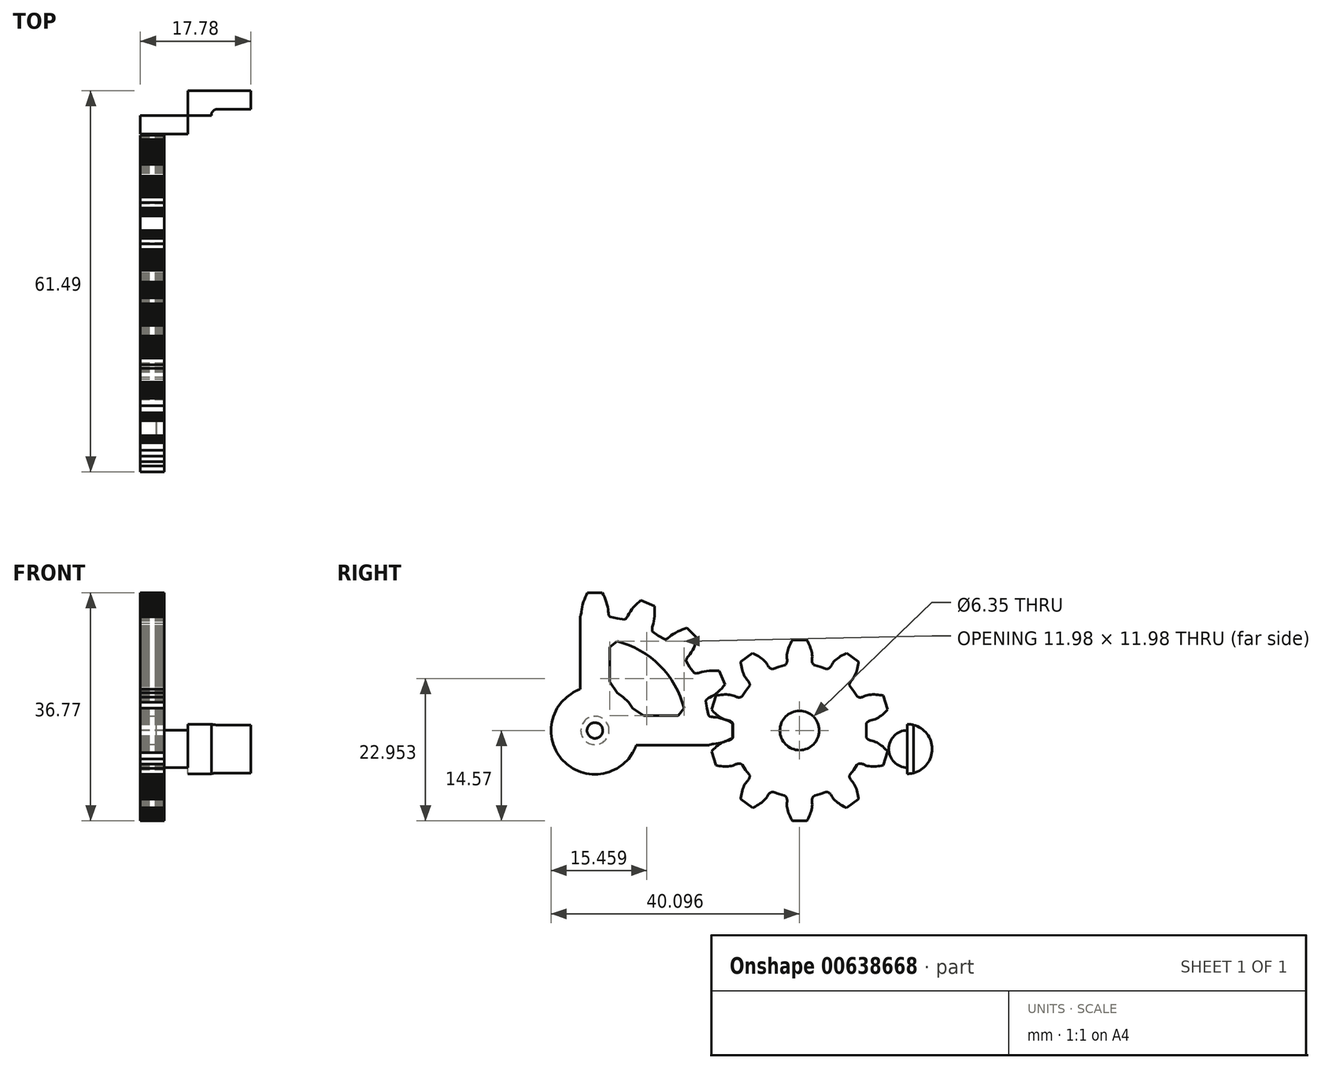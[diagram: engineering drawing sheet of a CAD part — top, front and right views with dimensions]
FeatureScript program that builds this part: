
annotation { "Feature Type Name" : "Feature", "Feature Type Description" : "" }
export const myFeature = defineFeature(function(context is Context, id is Id, definition is map)
    precondition{}
    {
        {
            var Q0;
            Q0=qCreatedBy(makeId("Right.planeOp"),FACE);
            var sketch = newSketch(context, id + "F0", { "sketchPlane" : qUnion([Q0])});
            skLineSegment(sketch, "E0", {"start": v(-32.36, 6.57) * mm, "end": v(-32.07, 5.41) * mm});
            skLineSegment(sketch, "E1", {"start": v(-32.07, 5.41) * mm, "end": v(-31.97, 5.33) * mm});
            skLineSegment(sketch, "E2", {"start": v(-31.97, 5.33) * mm, "end": v(-31.86, 5.27) * mm});
            skLineSegment(sketch, "E3", {"start": v(-31.86, 5.27) * mm, "end": v(-31.66, 5.2) * mm});
            skLineSegment(sketch, "E4", {"start": v(-31.66, 5.2) * mm, "end": v(-31.46, 5.16) * mm});
            skLineSegment(sketch, "E5", {"start": v(-31.46, 5.16) * mm, "end": v(-31.27, 5.14) * mm});
            skLineSegment(sketch, "E6", {"start": v(-31.27, 5.14) * mm, "end": v(-30.88, 5.1) * mm});
            skLineSegment(sketch, "E7", {"start": v(-30.88, 5.1) * mm, "end": v(-30.49, 5.04) * mm});
            skLineSegment(sketch, "E8", {"start": v(-30.49, 5.04) * mm, "end": v(-30.1, 4.95) * mm});
            skLineSegment(sketch, "E9", {"start": v(-30.1, 4.95) * mm, "end": v(-29.7, 4.83) * mm});
            skLineSegment(sketch, "E10", {"start": v(-29.7, 4.83) * mm, "end": v(-29.3, 4.68) * mm});
            skLineSegment(sketch, "E11", {"start": v(-29.3, 4.68) * mm, "end": v(-28.9, 4.52) * mm});
            skLineSegment(sketch, "E12", {"start": v(-28.9, 4.52) * mm, "end": v(-28.5, 4.34) * mm});
            skLineSegment(sketch, "E13", {"start": v(-28.5, 4.34) * mm, "end": v(-28.21, 4.19) * mm});
            skLineSegment(sketch, "E14", {"start": v(-28.21, 4.19) * mm, "end": v(-28.21, 1.77) * mm});
            skLineSegment(sketch, "E15", {"start": v(-28.21, 1.77) * mm, "end": v(-28.5, 1.62) * mm});
            skLineSegment(sketch, "E16", {"start": v(-28.5, 1.62) * mm, "end": v(-28.9, 1.44) * mm});
            skLineSegment(sketch, "E17", {"start": v(-28.9, 1.44) * mm, "end": v(-29.3, 1.28) * mm});
            skLineSegment(sketch, "E18", {"start": v(-29.3, 1.28) * mm, "end": v(-29.7, 1.13) * mm});
            skLineSegment(sketch, "E19", {"start": v(-29.7, 1.13) * mm, "end": v(-30.1, 1.01) * mm});
            skLineSegment(sketch, "E20", {"start": v(-30.1, 1.01) * mm, "end": v(-30.49, 0.92) * mm});
            skLineSegment(sketch, "E21", {"start": v(-30.49, 0.92) * mm, "end": v(-30.88, 0.85) * mm});
            skLineSegment(sketch, "E22", {"start": v(-30.88, 0.85) * mm, "end": v(-31.27, 0.82) * mm});
            skLineSegment(sketch, "E23", {"start": v(-31.27, 0.82) * mm, "end": v(-31.46, 0.8) * mm});
            skLineSegment(sketch, "E24", {"start": v(-31.46, 0.8) * mm, "end": v(-31.66, 0.76) * mm});
            skLineSegment(sketch, "E25", {"start": v(-31.66, 0.76) * mm, "end": v(-31.86, 0.69) * mm});
            skLineSegment(sketch, "E26", {"start": v(-31.86, 0.69) * mm, "end": v(-31.97, 0.63) * mm});
            skLineSegment(sketch, "E27", {"start": v(-31.97, 0.63) * mm, "end": v(-32.07, 0.55) * mm});
            skLineSegment(sketch, "E28", {"start": v(-32.07, 0.55) * mm, "end": v(-32.36, -0.61) * mm});
            skLineSegment(sketch, "E29", {"start": v(-32.36, -0.61) * mm, "end": v(-32.54, -1.79) * mm});
            skLineSegment(sketch, "E30", {"start": v(-32.54, -1.79) * mm, "end": v(-32.47, -1.9) * mm});
            skLineSegment(sketch, "E31", {"start": v(-32.47, -1.9) * mm, "end": v(-32.4, -2) * mm});
            skLineSegment(sketch, "E32", {"start": v(-32.4, -2) * mm, "end": v(-32.24, -2.15) * mm});
            skLineSegment(sketch, "E33", {"start": v(-32.24, -2.15) * mm, "end": v(-32.07, -2.26) * mm});
            skLineSegment(sketch, "E34", {"start": v(-32.07, -2.26) * mm, "end": v(-31.9, -2.35) * mm});
            skLineSegment(sketch, "E35", {"start": v(-31.9, -2.35) * mm, "end": v(-31.55, -2.53) * mm});
            skLineSegment(sketch, "E36", {"start": v(-31.55, -2.53) * mm, "end": v(-31.22, -2.74) * mm});
            skLineSegment(sketch, "E37", {"start": v(-31.22, -2.74) * mm, "end": v(-30.89, -2.98) * mm});
            skLineSegment(sketch, "E38", {"start": v(-30.89, -2.98) * mm, "end": v(-30.57, -3.24) * mm});
            skLineSegment(sketch, "E39", {"start": v(-30.57, -3.24) * mm, "end": v(-30.26, -3.52) * mm});
            skLineSegment(sketch, "E40", {"start": v(-30.26, -3.52) * mm, "end": v(-29.95, -3.83) * mm});
            skLineSegment(sketch, "E41", {"start": v(-29.95, -3.83) * mm, "end": v(-29.66, -4.15) * mm});
            skLineSegment(sketch, "E42", {"start": v(-29.66, -4.15) * mm, "end": v(-29.44, -4.4) * mm});
            skLineSegment(sketch, "E43", {"start": v(-29.44, -4.4) * mm, "end": v(-30.37, -6.63) * mm});
            skLineSegment(sketch, "E44", {"start": v(-30.37, -6.63) * mm, "end": v(-30.7, -6.66) * mm});
            skLineSegment(sketch, "E45", {"start": v(-30.7, -6.66) * mm, "end": v(-31.13, -6.68) * mm});
            skLineSegment(sketch, "E46", {"start": v(-31.13, -6.68) * mm, "end": v(-31.56, -6.67) * mm});
            skLineSegment(sketch, "E47", {"start": v(-31.56, -6.67) * mm, "end": v(-31.98, -6.65) * mm});
            skLineSegment(sketch, "E48", {"start": v(-31.98, -6.65) * mm, "end": v(-32.4, -6.61) * mm});
            skLineSegment(sketch, "E49", {"start": v(-32.4, -6.61) * mm, "end": v(-32.8, -6.55) * mm});
            skLineSegment(sketch, "E50", {"start": v(-32.8, -6.55) * mm, "end": v(-33.18, -6.46) * mm});
            skLineSegment(sketch, "E51", {"start": v(-33.18, -6.46) * mm, "end": v(-33.55, -6.34) * mm});
            skLineSegment(sketch, "E52", {"start": v(-33.55, -6.34) * mm, "end": v(-33.74, -6.28) * mm});
            skLineSegment(sketch, "E53", {"start": v(-33.74, -6.28) * mm, "end": v(-33.94, -6.25) * mm});
            skLineSegment(sketch, "E54", {"start": v(-33.94, -6.25) * mm, "end": v(-34.15, -6.24) * mm});
            skLineSegment(sketch, "E55", {"start": v(-34.15, -6.24) * mm, "end": v(-34.27, -6.25) * mm});
            skLineSegment(sketch, "E56", {"start": v(-34.27, -6.25) * mm, "end": v(-34.4, -6.29) * mm});
            skLineSegment(sketch, "E57", {"start": v(-34.4, -6.29) * mm, "end": v(-35.11, -7.25) * mm});
            skLineSegment(sketch, "E58", {"start": v(-35.11, -7.25) * mm, "end": v(-35.72, -8.27) * mm});
            skLineSegment(sketch, "E59", {"start": v(-35.72, -8.27) * mm, "end": v(-35.7, -8.4) * mm});
            skLineSegment(sketch, "E60", {"start": v(-35.7, -8.4) * mm, "end": v(-35.68, -8.52) * mm});
            skLineSegment(sketch, "E61", {"start": v(-35.68, -8.52) * mm, "end": v(-35.58, -8.71) * mm});
            skLineSegment(sketch, "E62", {"start": v(-35.58, -8.71) * mm, "end": v(-35.47, -8.88) * mm});
            skLineSegment(sketch, "E63", {"start": v(-35.47, -8.88) * mm, "end": v(-35.35, -9.03) * mm});
            skLineSegment(sketch, "E64", {"start": v(-35.35, -9.03) * mm, "end": v(-35.1, -9.33) * mm});
            skLineSegment(sketch, "E65", {"start": v(-35.1, -9.33) * mm, "end": v(-34.87, -9.65) * mm});
            skLineSegment(sketch, "E66", {"start": v(-34.87, -9.65) * mm, "end": v(-34.66, -10) * mm});
            skLineSegment(sketch, "E67", {"start": v(-34.66, -10) * mm, "end": v(-34.46, -10.36) * mm});
            skLineSegment(sketch, "E68", {"start": v(-34.46, -10.36) * mm, "end": v(-34.28, -10.74) * mm});
            skLineSegment(sketch, "E69", {"start": v(-34.28, -10.74) * mm, "end": v(-34.11, -11.14) * mm});
            skLineSegment(sketch, "E70", {"start": v(-34.11, -11.14) * mm, "end": v(-33.96, -11.55) * mm});
            skLineSegment(sketch, "E71", {"start": v(-33.96, -11.55) * mm, "end": v(-33.86, -11.86) * mm});
            skLineSegment(sketch, "E72", {"start": v(-33.86, -11.86) * mm, "end": v(-35.57, -13.57) * mm});
            skLineSegment(sketch, "E73", {"start": v(-35.57, -13.57) * mm, "end": v(-35.89, -13.47) * mm});
            skLineSegment(sketch, "E74", {"start": v(-35.89, -13.47) * mm, "end": v(-36.3, -13.32) * mm});
            skLineSegment(sketch, "E75", {"start": v(-36.3, -13.32) * mm, "end": v(-36.7, -13.15) * mm});
            skLineSegment(sketch, "E76", {"start": v(-36.7, -13.15) * mm, "end": v(-37.07, -12.97) * mm});
            skLineSegment(sketch, "E77", {"start": v(-37.07, -12.97) * mm, "end": v(-37.43, -12.78) * mm});
            skLineSegment(sketch, "E78", {"start": v(-37.43, -12.78) * mm, "end": v(-37.78, -12.57) * mm});
            skLineSegment(sketch, "E79", {"start": v(-37.78, -12.57) * mm, "end": v(-38.1, -12.34) * mm});
            skLineSegment(sketch, "E80", {"start": v(-38.1, -12.34) * mm, "end": v(-38.4, -12.08) * mm});
            skLineSegment(sketch, "E81", {"start": v(-38.4, -12.08) * mm, "end": v(-38.55, -11.96) * mm});
            skLineSegment(sketch, "E82", {"start": v(-38.55, -11.96) * mm, "end": v(-38.72, -11.85) * mm});
            skLineSegment(sketch, "E83", {"start": v(-38.72, -11.85) * mm, "end": v(-38.92, -11.76) * mm});
            skLineSegment(sketch, "E84", {"start": v(-38.92, -11.76) * mm, "end": v(-39.03, -11.73) * mm});
            skLineSegment(sketch, "E85", {"start": v(-39.03, -11.73) * mm, "end": v(-39.17, -11.71) * mm});
            skLineSegment(sketch, "E86", {"start": v(-39.17, -11.71) * mm, "end": v(-40.19, -12.32) * mm});
            skLineSegment(sketch, "E87", {"start": v(-40.19, -12.32) * mm, "end": v(-41.15, -13.03) * mm});
            skLineSegment(sketch, "E88", {"start": v(-41.15, -13.03) * mm, "end": v(-41.18, -13.17) * mm});
            skLineSegment(sketch, "E89", {"start": v(-41.18, -13.17) * mm, "end": v(-41.2, -13.28) * mm});
            skLineSegment(sketch, "E90", {"start": v(-41.2, -13.28) * mm, "end": v(-41.19, -13.5) * mm});
            skLineSegment(sketch, "E91", {"start": v(-41.19, -13.5) * mm, "end": v(-41.15, -13.7) * mm});
            skLineSegment(sketch, "E92", {"start": v(-41.15, -13.7) * mm, "end": v(-41.1, -13.88) * mm});
            skLineSegment(sketch, "E93", {"start": v(-41.1, -13.88) * mm, "end": v(-40.97, -14.25) * mm});
            skLineSegment(sketch, "E94", {"start": v(-40.97, -14.25) * mm, "end": v(-40.88, -14.64) * mm});
            skLineSegment(sketch, "E95", {"start": v(-40.88, -14.64) * mm, "end": v(-40.82, -15.04) * mm});
            skLineSegment(sketch, "E96", {"start": v(-40.82, -15.04) * mm, "end": v(-40.78, -15.45) * mm});
            skLineSegment(sketch, "E97", {"start": v(-40.78, -15.45) * mm, "end": v(-40.76, -15.87) * mm});
            skLineSegment(sketch, "E98", {"start": v(-40.76, -15.87) * mm, "end": v(-40.76, -16.3) * mm});
            skLineSegment(sketch, "E99", {"start": v(-40.76, -16.3) * mm, "end": v(-40.78, -16.74) * mm});
            skLineSegment(sketch, "E100", {"start": v(-40.78, -16.74) * mm, "end": v(-40.8, -17.07) * mm});
            skLineSegment(sketch, "E101", {"start": v(-40.8, -17.07) * mm, "end": v(-43.03, -18) * mm});
            skLineSegment(sketch, "E102", {"start": v(-43.03, -18) * mm, "end": v(-43.29, -17.78) * mm});
            skLineSegment(sketch, "E103", {"start": v(-43.29, -17.78) * mm, "end": v(-43.6, -17.48) * mm});
            skLineSegment(sketch, "E104", {"start": v(-43.6, -17.48) * mm, "end": v(-43.9, -17.18) * mm});
            skLineSegment(sketch, "E105", {"start": v(-43.9, -17.18) * mm, "end": v(-44.2, -16.87) * mm});
            skLineSegment(sketch, "E106", {"start": v(-44.2, -16.87) * mm, "end": v(-44.45, -16.55) * mm});
            skLineSegment(sketch, "E107", {"start": v(-44.45, -16.55) * mm, "end": v(-44.7, -16.22) * mm});
            skLineSegment(sketch, "E108", {"start": v(-44.7, -16.22) * mm, "end": v(-44.9, -15.88) * mm});
            skLineSegment(sketch, "E109", {"start": v(-44.9, -15.88) * mm, "end": v(-45.08, -15.53) * mm});
            skLineSegment(sketch, "E110", {"start": v(-45.08, -15.53) * mm, "end": v(-45.17, -15.36) * mm});
            skLineSegment(sketch, "E111", {"start": v(-45.17, -15.36) * mm, "end": v(-45.29, -15.2) * mm});
            skLineSegment(sketch, "E112", {"start": v(-45.29, -15.2) * mm, "end": v(-45.43, -15.04) * mm});
            skLineSegment(sketch, "E113", {"start": v(-45.43, -15.04) * mm, "end": v(-45.52, -14.96) * mm});
            skLineSegment(sketch, "E114", {"start": v(-45.52, -14.96) * mm, "end": v(-45.64, -14.9) * mm});
            skLineSegment(sketch, "E115", {"start": v(-45.64, -14.9) * mm, "end": v(-46.82, -15.07) * mm});
            skLineSegment(sketch, "E116", {"start": v(-46.82, -15.07) * mm, "end": v(-47.98, -15.36) * mm});
            skLineSegment(sketch, "E117", {"start": v(-47.98, -15.36) * mm, "end": v(-48.06, -15.47) * mm});
            skLineSegment(sketch, "E118", {"start": v(-48.06, -15.47) * mm, "end": v(-48.12, -15.57) * mm});
            skLineSegment(sketch, "E119", {"start": v(-48.12, -15.57) * mm, "end": v(-48.2, -15.77) * mm});
            skLineSegment(sketch, "E120", {"start": v(-48.2, -15.77) * mm, "end": v(-48.24, -15.97) * mm});
            skLineSegment(sketch, "E121", {"start": v(-48.24, -15.97) * mm, "end": v(-48.26, -16.17) * mm});
            skLineSegment(sketch, "E122", {"start": v(-48.26, -16.17) * mm, "end": v(-48.29, -16.55) * mm});
            skLineSegment(sketch, "E123", {"start": v(-48.29, -16.55) * mm, "end": v(-48.35, -16.95) * mm});
            skLineSegment(sketch, "E124", {"start": v(-48.35, -16.95) * mm, "end": v(-48.45, -17.34) * mm});
            skLineSegment(sketch, "E125", {"start": v(-48.45, -17.34) * mm, "end": v(-48.57, -17.74) * mm});
            skLineSegment(sketch, "E126", {"start": v(-48.57, -17.74) * mm, "end": v(-48.7, -18.13) * mm});
            skLineSegment(sketch, "E127", {"start": v(-48.7, -18.13) * mm, "end": v(-48.87, -18.53) * mm});
            skLineSegment(sketch, "E128", {"start": v(-48.87, -18.53) * mm, "end": v(-49.06, -18.93) * mm});
            skLineSegment(sketch, "E129", {"start": v(-49.06, -18.93) * mm, "end": v(-49.2, -19.22) * mm});
            skLineSegment(sketch, "E130", {"start": v(-49.2, -19.22) * mm, "end": v(-51.62, -19.22) * mm});
            skLineSegment(sketch, "E131", {"start": v(-51.62, -19.22) * mm, "end": v(-51.77, -18.93) * mm});
            skLineSegment(sketch, "E132", {"start": v(-51.77, -18.93) * mm, "end": v(-51.96, -18.53) * mm});
            skLineSegment(sketch, "E133", {"start": v(-51.96, -18.53) * mm, "end": v(-52.12, -18.13) * mm});
            skLineSegment(sketch, "E134", {"start": v(-52.12, -18.13) * mm, "end": v(-52.26, -17.74) * mm});
            skLineSegment(sketch, "E135", {"start": v(-52.26, -17.74) * mm, "end": v(-52.38, -17.34) * mm});
            skLineSegment(sketch, "E136", {"start": v(-52.38, -17.34) * mm, "end": v(-52.47, -16.95) * mm});
            skLineSegment(sketch, "E137", {"start": v(-52.47, -16.95) * mm, "end": v(-52.54, -16.55) * mm});
            skLineSegment(sketch, "E138", {"start": v(-52.54, -16.55) * mm, "end": v(-52.57, -16.17) * mm});
            skLineSegment(sketch, "E139", {"start": v(-52.57, -16.17) * mm, "end": v(-52.6, -15.97) * mm});
            skLineSegment(sketch, "E140", {"start": v(-52.6, -15.97) * mm, "end": v(-52.63, -15.77) * mm});
            skLineSegment(sketch, "E141", {"start": v(-52.63, -15.77) * mm, "end": v(-52.7, -15.57) * mm});
            skLineSegment(sketch, "E142", {"start": v(-52.7, -15.57) * mm, "end": v(-52.76, -15.47) * mm});
            skLineSegment(sketch, "E143", {"start": v(-52.76, -15.47) * mm, "end": v(-52.85, -15.36) * mm});
            skLineSegment(sketch, "E144", {"start": v(-52.85, -15.36) * mm, "end": v(-54, -15.07) * mm});
            skLineSegment(sketch, "E145", {"start": v(-54, -15.07) * mm, "end": v(-55.18, -14.9) * mm});
            skLineSegment(sketch, "E146", {"start": v(-55.18, -14.9) * mm, "end": v(-55.3, -14.96) * mm});
            skLineSegment(sketch, "E147", {"start": v(-55.3, -14.96) * mm, "end": v(-55.4, -15.04) * mm});
            skLineSegment(sketch, "E148", {"start": v(-55.4, -15.04) * mm, "end": v(-55.54, -15.2) * mm});
            skLineSegment(sketch, "E149", {"start": v(-55.54, -15.2) * mm, "end": v(-55.65, -15.36) * mm});
            skLineSegment(sketch, "E150", {"start": v(-55.65, -15.36) * mm, "end": v(-55.75, -15.53) * mm});
            skLineSegment(sketch, "E151", {"start": v(-55.75, -15.53) * mm, "end": v(-55.92, -15.88) * mm});
            skLineSegment(sketch, "E152", {"start": v(-55.92, -15.88) * mm, "end": v(-56.14, -16.22) * mm});
            skLineSegment(sketch, "E153", {"start": v(-56.14, -16.22) * mm, "end": v(-56.37, -16.55) * mm});
            skLineSegment(sketch, "E154", {"start": v(-56.37, -16.55) * mm, "end": v(-56.64, -16.87) * mm});
            skLineSegment(sketch, "E155", {"start": v(-56.64, -16.87) * mm, "end": v(-56.92, -17.18) * mm});
            skLineSegment(sketch, "E156", {"start": v(-56.92, -17.18) * mm, "end": v(-57.22, -17.48) * mm});
            skLineSegment(sketch, "E157", {"start": v(-57.22, -17.48) * mm, "end": v(-57.54, -17.78) * mm});
            skLineSegment(sketch, "E158", {"start": v(-57.54, -17.78) * mm, "end": v(-57.8, -18) * mm});
            skLineSegment(sketch, "E159", {"start": v(-57.8, -18) * mm, "end": v(-60.03, -17.07) * mm});
            skLineSegment(sketch, "E160", {"start": v(-60.03, -17.07) * mm, "end": v(-60.05, -16.74) * mm});
            skLineSegment(sketch, "E161", {"start": v(-60.05, -16.74) * mm, "end": v(-60.07, -16.3) * mm});
            skLineSegment(sketch, "E162", {"start": v(-60.07, -16.3) * mm, "end": v(-60.07, -15.87) * mm});
            skLineSegment(sketch, "E163", {"start": v(-60.07, -15.87) * mm, "end": v(-60.05, -15.45) * mm});
            skLineSegment(sketch, "E164", {"start": v(-60.05, -15.45) * mm, "end": v(-60, -15.04) * mm});
            skLineSegment(sketch, "E165", {"start": v(-60, -15.04) * mm, "end": v(-59.94, -14.64) * mm});
            skLineSegment(sketch, "E166", {"start": v(-59.94, -14.64) * mm, "end": v(-59.85, -14.25) * mm});
            skLineSegment(sketch, "E167", {"start": v(-59.85, -14.25) * mm, "end": v(-59.74, -13.88) * mm});
            skLineSegment(sketch, "E168", {"start": v(-59.74, -13.88) * mm, "end": v(-59.68, -13.7) * mm});
            skLineSegment(sketch, "E169", {"start": v(-59.68, -13.7) * mm, "end": v(-59.64, -13.5) * mm});
            skLineSegment(sketch, "E170", {"start": v(-59.64, -13.5) * mm, "end": v(-59.63, -13.28) * mm});
            skLineSegment(sketch, "E171", {"start": v(-59.63, -13.28) * mm, "end": v(-59.64, -13.17) * mm});
            skLineSegment(sketch, "E172", {"start": v(-59.64, -13.17) * mm, "end": v(-59.68, -13.03) * mm});
            skLineSegment(sketch, "E173", {"start": v(-59.68, -13.03) * mm, "end": v(-60.64, -12.32) * mm});
            skLineSegment(sketch, "E174", {"start": v(-60.64, -12.32) * mm, "end": v(-61.66, -11.71) * mm});
            skLineSegment(sketch, "E175", {"start": v(-61.66, -11.71) * mm, "end": v(-61.8, -11.73) * mm});
            skLineSegment(sketch, "E176", {"start": v(-61.8, -11.73) * mm, "end": v(-61.91, -11.76) * mm});
            skLineSegment(sketch, "E177", {"start": v(-61.91, -11.76) * mm, "end": v(-62.1, -11.85) * mm});
            skLineSegment(sketch, "E178", {"start": v(-62.1, -11.85) * mm, "end": v(-62.27, -11.96) * mm});
            skLineSegment(sketch, "E179", {"start": v(-62.27, -11.96) * mm, "end": v(-62.43, -12.08) * mm});
            skLineSegment(sketch, "E180", {"start": v(-62.43, -12.08) * mm, "end": v(-62.72, -12.34) * mm});
            skLineSegment(sketch, "E181", {"start": v(-62.72, -12.34) * mm, "end": v(-63.05, -12.57) * mm});
            skLineSegment(sketch, "E182", {"start": v(-63.05, -12.57) * mm, "end": v(-63.4, -12.78) * mm});
            skLineSegment(sketch, "E183", {"start": v(-63.4, -12.78) * mm, "end": v(-63.76, -12.97) * mm});
            skLineSegment(sketch, "E184", {"start": v(-63.76, -12.97) * mm, "end": v(-64.14, -13.15) * mm});
            skLineSegment(sketch, "E185", {"start": v(-64.14, -13.15) * mm, "end": v(-64.53, -13.32) * mm});
            skLineSegment(sketch, "E186", {"start": v(-64.53, -13.32) * mm, "end": v(-64.94, -13.47) * mm});
            skLineSegment(sketch, "E187", {"start": v(-64.94, -13.47) * mm, "end": v(-65.26, -13.57) * mm});
            skLineSegment(sketch, "E188", {"start": v(-65.26, -13.57) * mm, "end": v(-66.97, -11.86) * mm});
            skLineSegment(sketch, "E189", {"start": v(-66.97, -11.86) * mm, "end": v(-66.86, -11.55) * mm});
            skLineSegment(sketch, "E190", {"start": v(-66.86, -11.55) * mm, "end": v(-66.71, -11.14) * mm});
            skLineSegment(sketch, "E191", {"start": v(-66.71, -11.14) * mm, "end": v(-66.55, -10.74) * mm});
            skLineSegment(sketch, "E192", {"start": v(-66.55, -10.74) * mm, "end": v(-66.37, -10.36) * mm});
            skLineSegment(sketch, "E193", {"start": v(-66.37, -10.36) * mm, "end": v(-66.17, -10) * mm});
            skLineSegment(sketch, "E194", {"start": v(-66.17, -10) * mm, "end": v(-65.96, -9.65) * mm});
            skLineSegment(sketch, "E195", {"start": v(-65.96, -9.65) * mm, "end": v(-65.73, -9.33) * mm});
            skLineSegment(sketch, "E196", {"start": v(-65.73, -9.33) * mm, "end": v(-65.48, -9.03) * mm});
            skLineSegment(sketch, "E197", {"start": v(-65.48, -9.03) * mm, "end": v(-65.35, -8.88) * mm});
            skLineSegment(sketch, "E198", {"start": v(-65.35, -8.88) * mm, "end": v(-65.24, -8.71) * mm});
            skLineSegment(sketch, "E199", {"start": v(-65.24, -8.71) * mm, "end": v(-65.15, -8.52) * mm});
            skLineSegment(sketch, "E200", {"start": v(-65.15, -8.52) * mm, "end": v(-65.12, -8.4) * mm});
            skLineSegment(sketch, "E201", {"start": v(-65.12, -8.4) * mm, "end": v(-65.1, -8.27) * mm});
            skLineSegment(sketch, "E202", {"start": v(-65.1, -8.27) * mm, "end": v(-65.72, -7.25) * mm});
            skLineSegment(sketch, "E203", {"start": v(-65.72, -7.25) * mm, "end": v(-66.43, -6.29) * mm});
            skLineSegment(sketch, "E204", {"start": v(-66.43, -6.29) * mm, "end": v(-66.56, -6.25) * mm});
            skLineSegment(sketch, "E205", {"start": v(-66.56, -6.25) * mm, "end": v(-66.68, -6.24) * mm});
            skLineSegment(sketch, "E206", {"start": v(-66.68, -6.24) * mm, "end": v(-66.9, -6.25) * mm});
            skLineSegment(sketch, "E207", {"start": v(-66.9, -6.25) * mm, "end": v(-67.09, -6.28) * mm});
            skLineSegment(sketch, "E208", {"start": v(-67.09, -6.28) * mm, "end": v(-67.28, -6.34) * mm});
            skLineSegment(sketch, "E209", {"start": v(-67.28, -6.34) * mm, "end": v(-67.65, -6.46) * mm});
            skLineSegment(sketch, "E210", {"start": v(-67.65, -6.46) * mm, "end": v(-68.04, -6.55) * mm});
            skLineSegment(sketch, "E211", {"start": v(-68.04, -6.55) * mm, "end": v(-68.44, -6.61) * mm});
            skLineSegment(sketch, "E212", {"start": v(-68.44, -6.61) * mm, "end": v(-68.85, -6.65) * mm});
            skLineSegment(sketch, "E213", {"start": v(-68.85, -6.65) * mm, "end": v(-69.27, -6.67) * mm});
            skLineSegment(sketch, "E214", {"start": v(-69.27, -6.67) * mm, "end": v(-69.7, -6.68) * mm});
            skLineSegment(sketch, "E215", {"start": v(-69.7, -6.68) * mm, "end": v(-70.13, -6.66) * mm});
            skLineSegment(sketch, "E216", {"start": v(-70.13, -6.66) * mm, "end": v(-70.46, -6.63) * mm});
            skLineSegment(sketch, "E217", {"start": v(-70.46, -6.63) * mm, "end": v(-71.39, -4.4) * mm});
            skLineSegment(sketch, "E218", {"start": v(-71.39, -4.4) * mm, "end": v(-71.17, -4.15) * mm});
            skLineSegment(sketch, "E219", {"start": v(-71.17, -4.15) * mm, "end": v(-70.88, -3.83) * mm});
            skLineSegment(sketch, "E220", {"start": v(-70.88, -3.83) * mm, "end": v(-70.57, -3.52) * mm});
            skLineSegment(sketch, "E221", {"start": v(-70.57, -3.52) * mm, "end": v(-70.26, -3.24) * mm});
            skLineSegment(sketch, "E222", {"start": v(-70.26, -3.24) * mm, "end": v(-69.94, -2.98) * mm});
            skLineSegment(sketch, "E223", {"start": v(-69.94, -2.98) * mm, "end": v(-69.61, -2.74) * mm});
            skLineSegment(sketch, "E224", {"start": v(-69.61, -2.74) * mm, "end": v(-69.28, -2.53) * mm});
            skLineSegment(sketch, "E225", {"start": v(-69.28, -2.53) * mm, "end": v(-68.93, -2.35) * mm});
            skLineSegment(sketch, "E226", {"start": v(-68.93, -2.35) * mm, "end": v(-68.76, -2.26) * mm});
            skLineSegment(sketch, "E227", {"start": v(-68.76, -2.26) * mm, "end": v(-68.59, -2.15) * mm});
            skLineSegment(sketch, "E228", {"start": v(-68.59, -2.15) * mm, "end": v(-68.43, -2) * mm});
            skLineSegment(sketch, "E229", {"start": v(-68.43, -2) * mm, "end": v(-68.36, -1.9) * mm});
            skLineSegment(sketch, "E230", {"start": v(-68.36, -1.9) * mm, "end": v(-68.3, -1.79) * mm});
            skLineSegment(sketch, "E231", {"start": v(-68.3, -1.79) * mm, "end": v(-68.47, -0.61) * mm});
            skLineSegment(sketch, "E232", {"start": v(-68.47, -0.61) * mm, "end": v(-68.75, 0.55) * mm});
            skLineSegment(sketch, "E233", {"start": v(-68.75, 0.55) * mm, "end": v(-68.86, 0.63) * mm});
            skLineSegment(sketch, "E234", {"start": v(-68.86, 0.63) * mm, "end": v(-68.97, 0.69) * mm});
            skLineSegment(sketch, "E235", {"start": v(-68.97, 0.69) * mm, "end": v(-69.17, 0.76) * mm});
            skLineSegment(sketch, "E236", {"start": v(-69.17, 0.76) * mm, "end": v(-69.36, 0.8) * mm});
            skLineSegment(sketch, "E237", {"start": v(-69.36, 0.8) * mm, "end": v(-69.56, 0.82) * mm});
            skLineSegment(sketch, "E238", {"start": v(-69.56, 0.82) * mm, "end": v(-69.95, 0.85) * mm});
            skLineSegment(sketch, "E239", {"start": v(-69.95, 0.85) * mm, "end": v(-70.34, 0.92) * mm});
            skLineSegment(sketch, "E240", {"start": v(-70.34, 0.92) * mm, "end": v(-70.74, 1.01) * mm});
            skLineSegment(sketch, "E241", {"start": v(-70.74, 1.01) * mm, "end": v(-71.13, 1.13) * mm});
            skLineSegment(sketch, "E242", {"start": v(-71.13, 1.13) * mm, "end": v(-71.53, 1.28) * mm});
            skLineSegment(sketch, "E243", {"start": v(-71.53, 1.28) * mm, "end": v(-71.92, 1.44) * mm});
            skLineSegment(sketch, "E244", {"start": v(-71.92, 1.44) * mm, "end": v(-72.32, 1.62) * mm});
            skLineSegment(sketch, "E245", {"start": v(-72.32, 1.62) * mm, "end": v(-72.62, 1.77) * mm});
            skLineSegment(sketch, "E246", {"start": v(-72.62, 1.77) * mm, "end": v(-72.62, 4.19) * mm});
            skLineSegment(sketch, "E247", {"start": v(-72.62, 4.19) * mm, "end": v(-72.32, 4.34) * mm});
            skLineSegment(sketch, "E248", {"start": v(-72.32, 4.34) * mm, "end": v(-71.92, 4.52) * mm});
            skLineSegment(sketch, "E249", {"start": v(-71.92, 4.52) * mm, "end": v(-71.53, 4.68) * mm});
            skLineSegment(sketch, "E250", {"start": v(-71.53, 4.68) * mm, "end": v(-71.13, 4.83) * mm});
            skLineSegment(sketch, "E251", {"start": v(-71.13, 4.83) * mm, "end": v(-70.74, 4.95) * mm});
            skLineSegment(sketch, "E252", {"start": v(-70.74, 4.95) * mm, "end": v(-70.34, 5.04) * mm});
            skLineSegment(sketch, "E253", {"start": v(-70.34, 5.04) * mm, "end": v(-69.95, 5.1) * mm});
            skLineSegment(sketch, "E254", {"start": v(-69.95, 5.1) * mm, "end": v(-69.56, 5.14) * mm});
            skLineSegment(sketch, "E255", {"start": v(-69.56, 5.14) * mm, "end": v(-69.36, 5.16) * mm});
            skLineSegment(sketch, "E256", {"start": v(-69.36, 5.16) * mm, "end": v(-69.17, 5.2) * mm});
            skLineSegment(sketch, "E257", {"start": v(-69.17, 5.2) * mm, "end": v(-68.97, 5.27) * mm});
            skLineSegment(sketch, "E258", {"start": v(-68.97, 5.27) * mm, "end": v(-68.86, 5.33) * mm});
            skLineSegment(sketch, "E259", {"start": v(-68.86, 5.33) * mm, "end": v(-68.75, 5.41) * mm});
            skLineSegment(sketch, "E260", {"start": v(-68.75, 5.41) * mm, "end": v(-68.47, 6.57) * mm});
            skLineSegment(sketch, "E261", {"start": v(-68.47, 6.57) * mm, "end": v(-68.3, 7.75) * mm});
            skLineSegment(sketch, "E262", {"start": v(-68.3, 7.75) * mm, "end": v(-68.36, 7.87) * mm});
            skLineSegment(sketch, "E263", {"start": v(-68.36, 7.87) * mm, "end": v(-68.43, 7.96) * mm});
            skLineSegment(sketch, "E264", {"start": v(-68.43, 7.96) * mm, "end": v(-68.59, 8.1) * mm});
            skLineSegment(sketch, "E265", {"start": v(-68.59, 8.1) * mm, "end": v(-68.76, 8.22) * mm});
            skLineSegment(sketch, "E266", {"start": v(-68.76, 8.22) * mm, "end": v(-68.93, 8.31) * mm});
            skLineSegment(sketch, "E267", {"start": v(-68.93, 8.31) * mm, "end": v(-69.28, 8.5) * mm});
            skLineSegment(sketch, "E268", {"start": v(-69.28, 8.5) * mm, "end": v(-69.61, 8.7) * mm});
            skLineSegment(sketch, "E269", {"start": v(-69.61, 8.7) * mm, "end": v(-69.94, 8.94) * mm});
            skLineSegment(sketch, "E270", {"start": v(-69.94, 8.94) * mm, "end": v(-70.26, 9.2) * mm});
            skLineSegment(sketch, "E271", {"start": v(-70.26, 9.2) * mm, "end": v(-70.57, 9.48) * mm});
            skLineSegment(sketch, "E272", {"start": v(-70.57, 9.48) * mm, "end": v(-70.88, 9.79) * mm});
            skLineSegment(sketch, "E273", {"start": v(-70.88, 9.79) * mm, "end": v(-71.17, 10.1) * mm});
            skLineSegment(sketch, "E274", {"start": v(-71.17, 10.1) * mm, "end": v(-71.39, 10.36) * mm});
            skLineSegment(sketch, "E275", {"start": v(-71.39, 10.36) * mm, "end": v(-70.46, 12.6) * mm});
            skLineSegment(sketch, "E276", {"start": v(-70.46, 12.6) * mm, "end": v(-70.13, 12.62) * mm});
            skLineSegment(sketch, "E277", {"start": v(-70.13, 12.62) * mm, "end": v(-69.7, 12.64) * mm});
            skLineSegment(sketch, "E278", {"start": v(-69.7, 12.64) * mm, "end": v(-69.27, 12.63) * mm});
            skLineSegment(sketch, "E279", {"start": v(-69.27, 12.63) * mm, "end": v(-68.85, 12.61) * mm});
            skLineSegment(sketch, "E280", {"start": v(-68.85, 12.61) * mm, "end": v(-68.44, 12.57) * mm});
            skLineSegment(sketch, "E281", {"start": v(-68.44, 12.57) * mm, "end": v(-68.04, 12.5) * mm});
            skLineSegment(sketch, "E282", {"start": v(-68.04, 12.5) * mm, "end": v(-67.65, 12.42) * mm});
            skLineSegment(sketch, "E283", {"start": v(-67.65, 12.42) * mm, "end": v(-67.28, 12.3) * mm});
            skLineSegment(sketch, "E284", {"start": v(-67.28, 12.3) * mm, "end": v(-67.09, 12.24) * mm});
            skLineSegment(sketch, "E285", {"start": v(-67.09, 12.24) * mm, "end": v(-66.9, 12.2) * mm});
            skLineSegment(sketch, "E286", {"start": v(-66.9, 12.2) * mm, "end": v(-66.68, 12.2) * mm});
            skLineSegment(sketch, "E287", {"start": v(-66.68, 12.2) * mm, "end": v(-66.56, 12.2) * mm});
            skLineSegment(sketch, "E288", {"start": v(-66.56, 12.2) * mm, "end": v(-66.43, 12.25) * mm});
            skLineSegment(sketch, "E289", {"start": v(-66.43, 12.25) * mm, "end": v(-65.72, 13.2) * mm});
            skLineSegment(sketch, "E290", {"start": v(-65.72, 13.2) * mm, "end": v(-65.1, 14.23) * mm});
            skLineSegment(sketch, "E291", {"start": v(-65.1, 14.23) * mm, "end": v(-65.12, 14.36) * mm});
            skLineSegment(sketch, "E292", {"start": v(-65.12, 14.36) * mm, "end": v(-65.15, 14.48) * mm});
            skLineSegment(sketch, "E293", {"start": v(-65.15, 14.48) * mm, "end": v(-65.24, 14.67) * mm});
            skLineSegment(sketch, "E294", {"start": v(-65.24, 14.67) * mm, "end": v(-65.35, 14.84) * mm});
            skLineSegment(sketch, "E295", {"start": v(-65.35, 14.84) * mm, "end": v(-65.48, 15) * mm});
            skLineSegment(sketch, "E296", {"start": v(-65.48, 15) * mm, "end": v(-65.73, 15.29) * mm});
            skLineSegment(sketch, "E297", {"start": v(-65.73, 15.29) * mm, "end": v(-65.96, 15.61) * mm});
            skLineSegment(sketch, "E298", {"start": v(-65.96, 15.61) * mm, "end": v(-66.17, 15.96) * mm});
            skLineSegment(sketch, "E299", {"start": v(-66.17, 15.96) * mm, "end": v(-66.37, 16.32) * mm});
            skLineSegment(sketch, "E300", {"start": v(-66.37, 16.32) * mm, "end": v(-66.55, 16.7) * mm});
            skLineSegment(sketch, "E301", {"start": v(-66.55, 16.7) * mm, "end": v(-66.71, 17.1) * mm});
            skLineSegment(sketch, "E302", {"start": v(-66.71, 17.1) * mm, "end": v(-66.86, 17.5) * mm});
            skLineSegment(sketch, "E303", {"start": v(-66.86, 17.5) * mm, "end": v(-66.97, 17.82) * mm});
            skLineSegment(sketch, "E304", {"start": v(-66.97, 17.82) * mm, "end": v(-65.26, 19.53) * mm});
            skLineSegment(sketch, "E305", {"start": v(-65.26, 19.53) * mm, "end": v(-64.94, 19.43) * mm});
            skLineSegment(sketch, "E306", {"start": v(-64.94, 19.43) * mm, "end": v(-64.53, 19.28) * mm});
            skLineSegment(sketch, "E307", {"start": v(-64.53, 19.28) * mm, "end": v(-64.14, 19.11) * mm});
            skLineSegment(sketch, "E308", {"start": v(-64.14, 19.11) * mm, "end": v(-63.76, 18.93) * mm});
            skLineSegment(sketch, "E309", {"start": v(-63.76, 18.93) * mm, "end": v(-63.4, 18.74) * mm});
            skLineSegment(sketch, "E310", {"start": v(-63.4, 18.74) * mm, "end": v(-63.05, 18.53) * mm});
            skLineSegment(sketch, "E311", {"start": v(-63.05, 18.53) * mm, "end": v(-62.72, 18.3) * mm});
            skLineSegment(sketch, "E312", {"start": v(-62.72, 18.3) * mm, "end": v(-62.43, 18.04) * mm});
            skLineSegment(sketch, "E313", {"start": v(-62.43, 18.04) * mm, "end": v(-62.27, 17.92) * mm});
            skLineSegment(sketch, "E314", {"start": v(-62.27, 17.92) * mm, "end": v(-62.1, 17.8) * mm});
            skLineSegment(sketch, "E315", {"start": v(-62.1, 17.8) * mm, "end": v(-61.91, 17.72) * mm});
            skLineSegment(sketch, "E316", {"start": v(-61.91, 17.72) * mm, "end": v(-61.8, 17.69) * mm});
            skLineSegment(sketch, "E317", {"start": v(-61.8, 17.69) * mm, "end": v(-61.66, 17.67) * mm});
            skLineSegment(sketch, "E318", {"start": v(-61.66, 17.67) * mm, "end": v(-60.64, 18.28) * mm});
            skLineSegment(sketch, "E319", {"start": v(-60.64, 18.28) * mm, "end": v(-59.68, 19) * mm});
            skLineSegment(sketch, "E320", {"start": v(-59.68, 19) * mm, "end": v(-59.64, 19.12) * mm});
            skLineSegment(sketch, "E321", {"start": v(-59.64, 19.12) * mm, "end": v(-59.63, 19.24) * mm});
            skLineSegment(sketch, "E322", {"start": v(-59.63, 19.24) * mm, "end": v(-59.64, 19.46) * mm});
            skLineSegment(sketch, "E323", {"start": v(-59.64, 19.46) * mm, "end": v(-59.68, 19.65) * mm});
            skLineSegment(sketch, "E324", {"start": v(-59.68, 19.65) * mm, "end": v(-59.74, 19.84) * mm});
            skLineSegment(sketch, "E325", {"start": v(-59.74, 19.84) * mm, "end": v(-59.85, 20.21) * mm});
            skLineSegment(sketch, "E326", {"start": v(-59.85, 20.21) * mm, "end": v(-59.94, 20.6) * mm});
            skLineSegment(sketch, "E327", {"start": v(-59.94, 20.6) * mm, "end": v(-60, 21) * mm});
            skLineSegment(sketch, "E328", {"start": v(-60, 21) * mm, "end": v(-60.05, 21.41) * mm});
            skLineSegment(sketch, "E329", {"start": v(-60.05, 21.41) * mm, "end": v(-60.07, 21.83) * mm});
            skLineSegment(sketch, "E330", {"start": v(-60.07, 21.83) * mm, "end": v(-60.07, 22.26) * mm});
            skLineSegment(sketch, "E331", {"start": v(-60.07, 22.26) * mm, "end": v(-60.05, 22.7) * mm});
            skLineSegment(sketch, "E332", {"start": v(-60.05, 22.7) * mm, "end": v(-60.03, 23.03) * mm});
            skLineSegment(sketch, "E333", {"start": v(-60.03, 23.03) * mm, "end": v(-57.8, 23.95) * mm});
            skLineSegment(sketch, "E334", {"start": v(-57.8, 23.95) * mm, "end": v(-57.54, 23.74) * mm});
            skLineSegment(sketch, "E335", {"start": v(-57.54, 23.74) * mm, "end": v(-57.22, 23.44) * mm});
            skLineSegment(sketch, "E336", {"start": v(-57.22, 23.44) * mm, "end": v(-56.92, 23.14) * mm});
            skLineSegment(sketch, "E337", {"start": v(-56.92, 23.14) * mm, "end": v(-56.64, 22.83) * mm});
            skLineSegment(sketch, "E338", {"start": v(-56.64, 22.83) * mm, "end": v(-56.37, 22.5) * mm});
            skLineSegment(sketch, "E339", {"start": v(-56.37, 22.5) * mm, "end": v(-56.14, 22.18) * mm});
            skLineSegment(sketch, "E340", {"start": v(-56.14, 22.18) * mm, "end": v(-55.92, 21.84) * mm});
            skLineSegment(sketch, "E341", {"start": v(-55.92, 21.84) * mm, "end": v(-55.75, 21.5) * mm});
            skLineSegment(sketch, "E342", {"start": v(-55.75, 21.5) * mm, "end": v(-55.65, 21.32) * mm});
            skLineSegment(sketch, "E343", {"start": v(-55.65, 21.32) * mm, "end": v(-55.54, 21.15) * mm});
            skLineSegment(sketch, "E344", {"start": v(-55.54, 21.15) * mm, "end": v(-55.4, 21) * mm});
            skLineSegment(sketch, "E345", {"start": v(-55.4, 21) * mm, "end": v(-55.3, 20.92) * mm});
            skLineSegment(sketch, "E346", {"start": v(-55.3, 20.92) * mm, "end": v(-55.18, 20.86) * mm});
            skLineSegment(sketch, "E347", {"start": v(-55.18, 20.86) * mm, "end": v(-54, 21.03) * mm});
            skLineSegment(sketch, "E348", {"start": v(-54, 21.03) * mm, "end": v(-52.85, 21.32) * mm});
            skLineSegment(sketch, "E349", {"start": v(-52.85, 21.32) * mm, "end": v(-52.76, 21.43) * mm});
            skLineSegment(sketch, "E350", {"start": v(-52.76, 21.43) * mm, "end": v(-52.7, 21.53) * mm});
            skLineSegment(sketch, "E351", {"start": v(-52.7, 21.53) * mm, "end": v(-52.63, 21.73) * mm});
            skLineSegment(sketch, "E352", {"start": v(-52.63, 21.73) * mm, "end": v(-52.6, 21.93) * mm});
            skLineSegment(sketch, "E353", {"start": v(-52.6, 21.93) * mm, "end": v(-52.57, 22.13) * mm});
            skLineSegment(sketch, "E354", {"start": v(-52.57, 22.13) * mm, "end": v(-52.54, 22.51) * mm});
            skLineSegment(sketch, "E355", {"start": v(-52.54, 22.51) * mm, "end": v(-52.47, 22.9) * mm});
            skLineSegment(sketch, "E356", {"start": v(-52.47, 22.9) * mm, "end": v(-52.38, 23.3) * mm});
            skLineSegment(sketch, "E357", {"start": v(-52.38, 23.3) * mm, "end": v(-52.26, 23.7) * mm});
            skLineSegment(sketch, "E358", {"start": v(-52.26, 23.7) * mm, "end": v(-52.12, 24.1) * mm});
            skLineSegment(sketch, "E359", {"start": v(-52.12, 24.1) * mm, "end": v(-51.96, 24.49) * mm});
            skLineSegment(sketch, "E360", {"start": v(-51.96, 24.49) * mm, "end": v(-51.77, 24.88) * mm});
            skLineSegment(sketch, "E361", {"start": v(-51.77, 24.88) * mm, "end": v(-51.62, 25.18) * mm});
            skLineSegment(sketch, "E362", {"start": v(-51.62, 25.18) * mm, "end": v(-49.2, 25.18) * mm});
            skLineSegment(sketch, "E363", {"start": v(-49.2, 25.18) * mm, "end": v(-49.06, 24.88) * mm});
            skLineSegment(sketch, "E364", {"start": v(-49.06, 24.88) * mm, "end": v(-48.87, 24.49) * mm});
            skLineSegment(sketch, "E365", {"start": v(-48.87, 24.49) * mm, "end": v(-48.7, 24.1) * mm});
            skLineSegment(sketch, "E366", {"start": v(-48.7, 24.1) * mm, "end": v(-48.57, 23.7) * mm});
            skLineSegment(sketch, "E367", {"start": v(-48.57, 23.7) * mm, "end": v(-48.45, 23.3) * mm});
            skLineSegment(sketch, "E368", {"start": v(-48.45, 23.3) * mm, "end": v(-48.35, 22.9) * mm});
            skLineSegment(sketch, "E369", {"start": v(-48.35, 22.9) * mm, "end": v(-48.29, 22.51) * mm});
            skLineSegment(sketch, "E370", {"start": v(-48.29, 22.51) * mm, "end": v(-48.26, 22.13) * mm});
            skLineSegment(sketch, "E371", {"start": v(-48.26, 22.13) * mm, "end": v(-48.24, 21.93) * mm});
            skLineSegment(sketch, "E372", {"start": v(-48.24, 21.93) * mm, "end": v(-48.2, 21.73) * mm});
            skLineSegment(sketch, "E373", {"start": v(-48.2, 21.73) * mm, "end": v(-48.12, 21.53) * mm});
            skLineSegment(sketch, "E374", {"start": v(-48.12, 21.53) * mm, "end": v(-48.06, 21.43) * mm});
            skLineSegment(sketch, "E375", {"start": v(-48.06, 21.43) * mm, "end": v(-47.98, 21.32) * mm});
            skLineSegment(sketch, "E376", {"start": v(-47.98, 21.32) * mm, "end": v(-46.82, 21.03) * mm});
            skLineSegment(sketch, "E377", {"start": v(-46.82, 21.03) * mm, "end": v(-45.64, 20.86) * mm});
            skLineSegment(sketch, "E378", {"start": v(-45.64, 20.86) * mm, "end": v(-45.52, 20.92) * mm});
            skLineSegment(sketch, "E379", {"start": v(-45.52, 20.92) * mm, "end": v(-45.43, 21) * mm});
            skLineSegment(sketch, "E380", {"start": v(-45.43, 21) * mm, "end": v(-45.29, 21.15) * mm});
            skLineSegment(sketch, "E381", {"start": v(-45.29, 21.15) * mm, "end": v(-45.17, 21.32) * mm});
            skLineSegment(sketch, "E382", {"start": v(-45.17, 21.32) * mm, "end": v(-45.08, 21.5) * mm});
            skLineSegment(sketch, "E383", {"start": v(-45.08, 21.5) * mm, "end": v(-44.9, 21.84) * mm});
            skLineSegment(sketch, "E384", {"start": v(-44.9, 21.84) * mm, "end": v(-44.7, 22.18) * mm});
            skLineSegment(sketch, "E385", {"start": v(-44.7, 22.18) * mm, "end": v(-44.45, 22.5) * mm});
            skLineSegment(sketch, "E386", {"start": v(-44.45, 22.5) * mm, "end": v(-44.2, 22.83) * mm});
            skLineSegment(sketch, "E387", {"start": v(-44.2, 22.83) * mm, "end": v(-43.9, 23.14) * mm});
            skLineSegment(sketch, "E388", {"start": v(-43.9, 23.14) * mm, "end": v(-43.6, 23.44) * mm});
            skLineSegment(sketch, "E389", {"start": v(-43.6, 23.44) * mm, "end": v(-43.29, 23.74) * mm});
            skLineSegment(sketch, "E390", {"start": v(-43.29, 23.74) * mm, "end": v(-43.03, 23.95) * mm});
            skLineSegment(sketch, "E391", {"start": v(-43.03, 23.95) * mm, "end": v(-40.8, 23.03) * mm});
            skLineSegment(sketch, "E392", {"start": v(-40.8, 23.03) * mm, "end": v(-40.78, 22.7) * mm});
            skLineSegment(sketch, "E393", {"start": v(-40.78, 22.7) * mm, "end": v(-40.76, 22.26) * mm});
            skLineSegment(sketch, "E394", {"start": v(-40.76, 22.26) * mm, "end": v(-40.76, 21.83) * mm});
            skLineSegment(sketch, "E395", {"start": v(-40.76, 21.83) * mm, "end": v(-40.78, 21.41) * mm});
            skLineSegment(sketch, "E396", {"start": v(-40.78, 21.41) * mm, "end": v(-40.82, 21) * mm});
            skLineSegment(sketch, "E397", {"start": v(-40.82, 21) * mm, "end": v(-40.88, 20.6) * mm});
            skLineSegment(sketch, "E398", {"start": v(-40.88, 20.6) * mm, "end": v(-40.97, 20.21) * mm});
            skLineSegment(sketch, "E399", {"start": v(-40.97, 20.21) * mm, "end": v(-41.1, 19.84) * mm});
            skLineSegment(sketch, "E400", {"start": v(-41.1, 19.84) * mm, "end": v(-41.15, 19.65) * mm});
            skLineSegment(sketch, "E401", {"start": v(-41.15, 19.65) * mm, "end": v(-41.19, 19.46) * mm});
            skLineSegment(sketch, "E402", {"start": v(-41.19, 19.46) * mm, "end": v(-41.2, 19.24) * mm});
            skLineSegment(sketch, "E403", {"start": v(-41.2, 19.24) * mm, "end": v(-41.18, 19.12) * mm});
            skLineSegment(sketch, "E404", {"start": v(-41.18, 19.12) * mm, "end": v(-41.15, 19) * mm});
            skLineSegment(sketch, "E405", {"start": v(-41.15, 19) * mm, "end": v(-40.19, 18.28) * mm});
            skLineSegment(sketch, "E406", {"start": v(-40.19, 18.28) * mm, "end": v(-39.17, 17.67) * mm});
            skLineSegment(sketch, "E407", {"start": v(-39.17, 17.67) * mm, "end": v(-39.03, 17.69) * mm});
            skLineSegment(sketch, "E408", {"start": v(-39.03, 17.69) * mm, "end": v(-38.92, 17.72) * mm});
            skLineSegment(sketch, "E409", {"start": v(-38.92, 17.72) * mm, "end": v(-38.72, 17.8) * mm});
            skLineSegment(sketch, "E410", {"start": v(-38.72, 17.8) * mm, "end": v(-38.55, 17.92) * mm});
            skLineSegment(sketch, "E411", {"start": v(-38.55, 17.92) * mm, "end": v(-38.4, 18.04) * mm});
            skLineSegment(sketch, "E412", {"start": v(-38.4, 18.04) * mm, "end": v(-38.1, 18.3) * mm});
            skLineSegment(sketch, "E413", {"start": v(-38.1, 18.3) * mm, "end": v(-37.78, 18.53) * mm});
            skLineSegment(sketch, "E414", {"start": v(-37.78, 18.53) * mm, "end": v(-37.43, 18.74) * mm});
            skLineSegment(sketch, "E415", {"start": v(-37.43, 18.74) * mm, "end": v(-37.07, 18.93) * mm});
            skLineSegment(sketch, "E416", {"start": v(-37.07, 18.93) * mm, "end": v(-36.7, 19.11) * mm});
            skLineSegment(sketch, "E417", {"start": v(-36.7, 19.11) * mm, "end": v(-36.3, 19.28) * mm});
            skLineSegment(sketch, "E418", {"start": v(-36.3, 19.28) * mm, "end": v(-35.89, 19.43) * mm});
            skLineSegment(sketch, "E419", {"start": v(-35.89, 19.43) * mm, "end": v(-35.57, 19.53) * mm});
            skLineSegment(sketch, "E420", {"start": v(-35.57, 19.53) * mm, "end": v(-33.86, 17.82) * mm});
            skLineSegment(sketch, "E421", {"start": v(-33.86, 17.82) * mm, "end": v(-33.96, 17.5) * mm});
            skLineSegment(sketch, "E422", {"start": v(-33.96, 17.5) * mm, "end": v(-34.11, 17.1) * mm});
            skLineSegment(sketch, "E423", {"start": v(-34.11, 17.1) * mm, "end": v(-34.28, 16.7) * mm});
            skLineSegment(sketch, "E424", {"start": v(-34.28, 16.7) * mm, "end": v(-34.46, 16.32) * mm});
            skLineSegment(sketch, "E425", {"start": v(-34.46, 16.32) * mm, "end": v(-34.66, 15.96) * mm});
            skLineSegment(sketch, "E426", {"start": v(-34.66, 15.96) * mm, "end": v(-34.87, 15.61) * mm});
            skLineSegment(sketch, "E427", {"start": v(-34.87, 15.61) * mm, "end": v(-35.1, 15.29) * mm});
            skLineSegment(sketch, "E428", {"start": v(-35.1, 15.29) * mm, "end": v(-35.35, 15) * mm});
            skLineSegment(sketch, "E429", {"start": v(-35.35, 15) * mm, "end": v(-35.47, 14.84) * mm});
            skLineSegment(sketch, "E430", {"start": v(-35.47, 14.84) * mm, "end": v(-35.58, 14.67) * mm});
            skLineSegment(sketch, "E431", {"start": v(-35.58, 14.67) * mm, "end": v(-35.68, 14.48) * mm});
            skLineSegment(sketch, "E432", {"start": v(-35.68, 14.48) * mm, "end": v(-35.7, 14.36) * mm});
            skLineSegment(sketch, "E433", {"start": v(-35.7, 14.36) * mm, "end": v(-35.72, 14.23) * mm});
            skLineSegment(sketch, "E434", {"start": v(-35.72, 14.23) * mm, "end": v(-35.11, 13.2) * mm});
            skLineSegment(sketch, "E435", {"start": v(-35.11, 13.2) * mm, "end": v(-34.4, 12.25) * mm});
            skLineSegment(sketch, "E436", {"start": v(-34.4, 12.25) * mm, "end": v(-34.27, 12.2) * mm});
            skLineSegment(sketch, "E437", {"start": v(-34.27, 12.2) * mm, "end": v(-34.15, 12.2) * mm});
            skLineSegment(sketch, "E438", {"start": v(-34.15, 12.2) * mm, "end": v(-33.94, 12.2) * mm});
            skLineSegment(sketch, "E439", {"start": v(-33.94, 12.2) * mm, "end": v(-33.74, 12.24) * mm});
            skLineSegment(sketch, "E440", {"start": v(-33.74, 12.24) * mm, "end": v(-33.55, 12.3) * mm});
            skLineSegment(sketch, "E441", {"start": v(-33.55, 12.3) * mm, "end": v(-33.18, 12.42) * mm});
            skLineSegment(sketch, "E442", {"start": v(-33.18, 12.42) * mm, "end": v(-32.8, 12.5) * mm});
            skLineSegment(sketch, "E443", {"start": v(-32.8, 12.5) * mm, "end": v(-32.4, 12.57) * mm});
            skLineSegment(sketch, "E444", {"start": v(-32.4, 12.57) * mm, "end": v(-31.98, 12.61) * mm});
            skLineSegment(sketch, "E445", {"start": v(-31.98, 12.61) * mm, "end": v(-31.56, 12.63) * mm});
            skLineSegment(sketch, "E446", {"start": v(-31.56, 12.63) * mm, "end": v(-31.13, 12.64) * mm});
            skLineSegment(sketch, "E447", {"start": v(-31.13, 12.64) * mm, "end": v(-30.7, 12.62) * mm});
            skLineSegment(sketch, "E448", {"start": v(-30.7, 12.62) * mm, "end": v(-30.37, 12.6) * mm});
            skLineSegment(sketch, "E449", {"start": v(-30.37, 12.6) * mm, "end": v(-29.44, 10.36) * mm});
            skLineSegment(sketch, "E450", {"start": v(-29.44, 10.36) * mm, "end": v(-29.66, 10.1) * mm});
            skLineSegment(sketch, "E451", {"start": v(-29.66, 10.1) * mm, "end": v(-29.95, 9.79) * mm});
            skLineSegment(sketch, "E452", {"start": v(-29.95, 9.79) * mm, "end": v(-30.26, 9.48) * mm});
            skLineSegment(sketch, "E453", {"start": v(-30.26, 9.48) * mm, "end": v(-30.57, 9.2) * mm});
            skLineSegment(sketch, "E454", {"start": v(-30.57, 9.2) * mm, "end": v(-30.89, 8.94) * mm});
            skLineSegment(sketch, "E455", {"start": v(-30.89, 8.94) * mm, "end": v(-31.22, 8.7) * mm});
            skLineSegment(sketch, "E456", {"start": v(-31.22, 8.7) * mm, "end": v(-31.55, 8.5) * mm});
            skLineSegment(sketch, "E457", {"start": v(-31.55, 8.5) * mm, "end": v(-31.9, 8.31) * mm});
            skLineSegment(sketch, "E458", {"start": v(-31.9, 8.31) * mm, "end": v(-32.07, 8.22) * mm});
            skLineSegment(sketch, "E459", {"start": v(-32.07, 8.22) * mm, "end": v(-32.24, 8.1) * mm});
            skLineSegment(sketch, "E460", {"start": v(-32.24, 8.1) * mm, "end": v(-32.4, 7.96) * mm});
            skLineSegment(sketch, "E461", {"start": v(-32.4, 7.96) * mm, "end": v(-32.47, 7.87) * mm});
            skLineSegment(sketch, "E462", {"start": v(-32.47, 7.87) * mm, "end": v(-32.54, 7.75) * mm});
            skLineSegment(sketch, "E463", {"start": v(-32.54, 7.75) * mm, "end": v(-32.36, 6.57) * mm});
            skLineSegment(sketch, "E464", {"start": v(-42.56, 5.37) * mm, "end": v(-37, 5.37) * mm});
            skLineSegment(sketch, "E465", {"start": v(-37, 5.37) * mm, "end": v(-36.04, 6.57) * mm});
            skLineSegment(sketch, "E466", {"start": v(-36.04, 6.57) * mm, "end": v(-36.32, 7.53) * mm});
            skLineSegment(sketch, "E467", {"start": v(-36.32, 7.53) * mm, "end": v(-36.66, 8.47) * mm});
            skLineSegment(sketch, "E468", {"start": v(-36.66, 8.47) * mm, "end": v(-37.06, 9.4) * mm});
            skLineSegment(sketch, "E469", {"start": v(-37.06, 9.4) * mm, "end": v(-37.52, 10.28) * mm});
            skLineSegment(sketch, "E470", {"start": v(-37.52, 10.28) * mm, "end": v(-38.04, 11.13) * mm});
            skLineSegment(sketch, "E471", {"start": v(-38.04, 11.13) * mm, "end": v(-38.62, 11.95) * mm});
            skLineSegment(sketch, "E472", {"start": v(-38.62, 11.95) * mm, "end": v(-39.26, 12.72) * mm});
            skLineSegment(sketch, "E473", {"start": v(-39.26, 12.72) * mm, "end": v(-39.94, 13.46) * mm});
            skLineSegment(sketch, "E474", {"start": v(-39.94, 13.46) * mm, "end": v(-40.67, 14.14) * mm});
            skLineSegment(sketch, "E475", {"start": v(-40.67, 14.14) * mm, "end": v(-41.45, 14.77) * mm});
            skLineSegment(sketch, "E476", {"start": v(-41.45, 14.77) * mm, "end": v(-42.26, 15.35) * mm});
            skLineSegment(sketch, "E477", {"start": v(-42.26, 15.35) * mm, "end": v(-43.12, 15.87) * mm});
            skLineSegment(sketch, "E478", {"start": v(-43.12, 15.87) * mm, "end": v(-44, 16.34) * mm});
            skLineSegment(sketch, "E479", {"start": v(-44, 16.34) * mm, "end": v(-44.92, 16.74) * mm});
            skLineSegment(sketch, "E480", {"start": v(-44.92, 16.74) * mm, "end": v(-45.86, 17.08) * mm});
            skLineSegment(sketch, "E481", {"start": v(-45.86, 17.08) * mm, "end": v(-46.82, 17.35) * mm});
            skLineSegment(sketch, "E482", {"start": v(-46.82, 17.35) * mm, "end": v(-48.02, 16.4) * mm});
            skLineSegment(sketch, "E483", {"start": v(-48.02, 16.4) * mm, "end": v(-48.02, 10.83) * mm});
            skLineSegment(sketch, "E484", {"start": v(-48.02, 10.83) * mm, "end": v(-46.82, 9.07) * mm});
            skLineSegment(sketch, "E485", {"start": v(-46.82, 9.07) * mm, "end": v(-45.85, 8.39) * mm});
            skLineSegment(sketch, "E486", {"start": v(-45.85, 8.39) * mm, "end": v(-45, 7.54) * mm});
            skLineSegment(sketch, "E487", {"start": v(-45, 7.54) * mm, "end": v(-44.32, 6.57) * mm});
            skLineSegment(sketch, "E488", {"start": v(-44.32, 6.57) * mm, "end": v(-42.56, 5.37) * mm});
            skLineSegment(sketch, "E489", {"start": v(-52.8, 9.64) * mm, "end": v(-52.8, 21.33) * mm});
            skLineSegment(sketch, "E490", {"start": v(-52.8, 16.4) * mm, "end": v(-54, 17.35) * mm});
            skLineSegment(sketch, "E491", {"start": v(-54, 17.35) * mm, "end": v(-54.97, 17.08) * mm});
            skLineSegment(sketch, "E492", {"start": v(-54.97, 17.08) * mm, "end": v(-55.9, 16.74) * mm});
            skLineSegment(sketch, "E493", {"start": v(-55.9, 16.74) * mm, "end": v(-56.83, 16.34) * mm});
            skLineSegment(sketch, "E494", {"start": v(-56.83, 16.34) * mm, "end": v(-57.71, 15.87) * mm});
            skLineSegment(sketch, "E495", {"start": v(-57.71, 15.87) * mm, "end": v(-58.57, 15.35) * mm});
            skLineSegment(sketch, "E496", {"start": v(-58.57, 15.35) * mm, "end": v(-59.38, 14.77) * mm});
            skLineSegment(sketch, "E497", {"start": v(-59.38, 14.77) * mm, "end": v(-60.16, 14.14) * mm});
            skLineSegment(sketch, "E498", {"start": v(-60.16, 14.14) * mm, "end": v(-60.89, 13.46) * mm});
            skLineSegment(sketch, "E499", {"start": v(-60.89, 13.46) * mm, "end": v(-61.57, 12.72) * mm});
            skLineSegment(sketch, "E500", {"start": v(-61.57, 12.72) * mm, "end": v(-62.2, 11.95) * mm});
            skLineSegment(sketch, "E501", {"start": v(-62.2, 11.95) * mm, "end": v(-62.78, 11.13) * mm});
            skLineSegment(sketch, "E502", {"start": v(-62.78, 11.13) * mm, "end": v(-63.3, 10.28) * mm});
            skLineSegment(sketch, "E503", {"start": v(-63.3, 10.28) * mm, "end": v(-63.77, 9.4) * mm});
            skLineSegment(sketch, "E504", {"start": v(-63.77, 9.4) * mm, "end": v(-64.17, 8.47) * mm});
            skLineSegment(sketch, "E505", {"start": v(-64.17, 8.47) * mm, "end": v(-64.51, 7.53) * mm});
            skLineSegment(sketch, "E506", {"start": v(-64.51, 7.53) * mm, "end": v(-64.79, 6.57) * mm});
            skLineSegment(sketch, "E507", {"start": v(-64.79, 6.57) * mm, "end": v(-63.84, 5.37) * mm});
            skLineSegment(sketch, "E508", {"start": v(-63.84, 5.37) * mm, "end": v(-58.27, 5.37) * mm});
            skLineSegment(sketch, "E509", {"start": v(-58.27, 5.37) * mm, "end": v(-56.5, 6.57) * mm});
            skLineSegment(sketch, "E510", {"start": v(-56.5, 6.57) * mm, "end": v(-55.82, 7.54) * mm});
            skLineSegment(sketch, "E511", {"start": v(-55.82, 7.54) * mm, "end": v(-54.98, 8.39) * mm});
            skLineSegment(sketch, "E512", {"start": v(-54.98, 8.39) * mm, "end": v(-54, 9.07) * mm});
            skLineSegment(sketch, "E513", {"start": v(-54, 9.07) * mm, "end": v(-52.8, 10.83) * mm});
            skLineSegment(sketch, "E514", {"start": v(-58.27, 0.59) * mm, "end": v(-63.84, 0.59) * mm});
            skLineSegment(sketch, "E515", {"start": v(-63.84, 0.59) * mm, "end": v(-64.79, -0.61) * mm});
            skLineSegment(sketch, "E516", {"start": v(-64.79, -0.61) * mm, "end": v(-64.51, -1.57) * mm});
            skLineSegment(sketch, "E517", {"start": v(-64.51, -1.57) * mm, "end": v(-64.17, -2.51) * mm});
            skLineSegment(sketch, "E518", {"start": v(-64.17, -2.51) * mm, "end": v(-63.77, -3.43) * mm});
            skLineSegment(sketch, "E519", {"start": v(-63.77, -3.43) * mm, "end": v(-63.3, -4.32) * mm});
            skLineSegment(sketch, "E520", {"start": v(-63.3, -4.32) * mm, "end": v(-62.78, -5.17) * mm});
            skLineSegment(sketch, "E521", {"start": v(-62.78, -5.17) * mm, "end": v(-62.2, -5.99) * mm});
            skLineSegment(sketch, "E522", {"start": v(-62.2, -5.99) * mm, "end": v(-61.57, -6.76) * mm});
            skLineSegment(sketch, "E523", {"start": v(-61.57, -6.76) * mm, "end": v(-60.89, -7.5) * mm});
            skLineSegment(sketch, "E524", {"start": v(-60.89, -7.5) * mm, "end": v(-60.16, -8.18) * mm});
            skLineSegment(sketch, "E525", {"start": v(-60.16, -8.18) * mm, "end": v(-59.38, -8.81) * mm});
            skLineSegment(sketch, "E526", {"start": v(-59.38, -8.81) * mm, "end": v(-58.57, -9.4) * mm});
            skLineSegment(sketch, "E527", {"start": v(-58.57, -9.4) * mm, "end": v(-57.71, -9.91) * mm});
            skLineSegment(sketch, "E528", {"start": v(-57.71, -9.91) * mm, "end": v(-56.83, -10.38) * mm});
            skLineSegment(sketch, "E529", {"start": v(-56.83, -10.38) * mm, "end": v(-55.9, -10.78) * mm});
            skLineSegment(sketch, "E530", {"start": v(-55.9, -10.78) * mm, "end": v(-54.97, -11.12) * mm});
            skLineSegment(sketch, "E531", {"start": v(-54.97, -11.12) * mm, "end": v(-54, -11.4) * mm});
            skLineSegment(sketch, "E532", {"start": v(-54, -11.4) * mm, "end": v(-52.8, -10.44) * mm});
            skLineSegment(sketch, "E533", {"start": v(-52.8, -10.44) * mm, "end": v(-52.8, -4.87) * mm});
            skLineSegment(sketch, "E534", {"start": v(-52.8, -4.87) * mm, "end": v(-54, -3.11) * mm});
            skLineSegment(sketch, "E535", {"start": v(-54, -3.11) * mm, "end": v(-54.98, -2.43) * mm});
            skLineSegment(sketch, "E536", {"start": v(-54.98, -2.43) * mm, "end": v(-55.82, -1.58) * mm});
            skLineSegment(sketch, "E537", {"start": v(-55.82, -1.58) * mm, "end": v(-56.5, -0.61) * mm});
            skLineSegment(sketch, "E538", {"start": v(-56.5, -0.61) * mm, "end": v(-58.27, 0.59) * mm});
            skLineSegment(sketch, "E539", {"start": v(-48.02, -4.87) * mm, "end": v(-48.02, -10.44) * mm});
            skLineSegment(sketch, "E540", {"start": v(-48.02, -10.44) * mm, "end": v(-46.82, -11.4) * mm});
            skLineSegment(sketch, "E541", {"start": v(-46.82, -11.4) * mm, "end": v(-45.86, -11.12) * mm});
            skLineSegment(sketch, "E542", {"start": v(-45.86, -11.12) * mm, "end": v(-44.92, -10.78) * mm});
            skLineSegment(sketch, "E543", {"start": v(-44.92, -10.78) * mm, "end": v(-44, -10.38) * mm});
            skLineSegment(sketch, "E544", {"start": v(-44, -10.38) * mm, "end": v(-43.12, -9.91) * mm});
            skLineSegment(sketch, "E545", {"start": v(-43.12, -9.91) * mm, "end": v(-42.26, -9.4) * mm});
            skLineSegment(sketch, "E546", {"start": v(-42.26, -9.4) * mm, "end": v(-41.45, -8.81) * mm});
            skLineSegment(sketch, "E547", {"start": v(-41.45, -8.81) * mm, "end": v(-40.67, -8.18) * mm});
            skLineSegment(sketch, "E548", {"start": v(-40.67, -8.18) * mm, "end": v(-39.94, -7.5) * mm});
            skLineSegment(sketch, "E549", {"start": v(-39.94, -7.5) * mm, "end": v(-39.26, -6.76) * mm});
            skLineSegment(sketch, "E550", {"start": v(-39.26, -6.76) * mm, "end": v(-38.62, -5.99) * mm});
            skLineSegment(sketch, "E551", {"start": v(-38.62, -5.99) * mm, "end": v(-38.04, -5.17) * mm});
            skLineSegment(sketch, "E552", {"start": v(-38.04, -5.17) * mm, "end": v(-37.52, -4.32) * mm});
            skLineSegment(sketch, "E553", {"start": v(-37.52, -4.32) * mm, "end": v(-37.06, -3.43) * mm});
            skLineSegment(sketch, "E554", {"start": v(-37.06, -3.43) * mm, "end": v(-36.66, -2.51) * mm});
            skLineSegment(sketch, "E555", {"start": v(-36.66, -2.51) * mm, "end": v(-36.32, -1.57) * mm});
            skLineSegment(sketch, "E556", {"start": v(-36.32, -1.57) * mm, "end": v(-36.04, -0.61) * mm});
            skLineSegment(sketch, "E557", {"start": v(-36.04, -0.61) * mm, "end": v(-37, 0.59) * mm});
            skLineSegment(sketch, "E558", {"start": v(-32.06, 0.59) * mm, "end": v(-43.76, 0.59) * mm});
            skLineSegment(sketch, "E559", {"start": v(-42.56, 0.59) * mm, "end": v(-44.32, -0.61) * mm});
            skLineSegment(sketch, "E560", {"start": v(-44.32, -0.61) * mm, "end": v(-45, -1.58) * mm});
            skLineSegment(sketch, "E561", {"start": v(-45, -1.58) * mm, "end": v(-45.85, -2.43) * mm});
            skLineSegment(sketch, "E562", {"start": v(-45.85, -2.43) * mm, "end": v(-46.82, -3.11) * mm});
            skLineSegment(sketch, "E563", {"start": v(-46.82, -3.11) * mm, "end": v(-48.02, -4.87) * mm});
            skCircle(sketch, "E564", {"center": v(-50.41, 2.98) * mm, "radius": 2.29 * mm});
            skLineSegment(sketch, "E565", {"start": v(-28.14, 3.92) * mm, "end": v(-28.18, 4.13) * mm});
            skLineSegment(sketch, "E566", {"start": v(-28.18, 4.13) * mm, "end": v(-28.24, 4.22) * mm});
            skLineSegment(sketch, "E567", {"start": v(-28.24, 4.22) * mm, "end": v(-28.3, 4.29) * mm});
            skLineSegment(sketch, "E568", {"start": v(-28.3, 4.29) * mm, "end": v(-28.35, 4.34) * mm});
            skLineSegment(sketch, "E569", {"start": v(-28.35, 4.34) * mm, "end": v(-28.4, 4.39) * mm});
            skLineSegment(sketch, "E570", {"start": v(-28.4, 4.39) * mm, "end": v(-28.53, 4.46) * mm});
            skLineSegment(sketch, "E571", {"start": v(-28.53, 4.46) * mm, "end": v(-28.65, 4.52) * mm});
            skLineSegment(sketch, "E572", {"start": v(-28.65, 4.52) * mm, "end": v(-28.77, 4.57) * mm});
            skLineSegment(sketch, "E573", {"start": v(-28.77, 4.57) * mm, "end": v(-28.9, 4.6) * mm});
            skLineSegment(sketch, "E574", {"start": v(-28.9, 4.6) * mm, "end": v(-29.14, 4.66) * mm});
            skLineSegment(sketch, "E575", {"start": v(-29.14, 4.66) * mm, "end": v(-29.4, 4.72) * mm});
            skLineSegment(sketch, "E576", {"start": v(-29.4, 4.72) * mm, "end": v(-29.64, 4.82) * mm});
            skLineSegment(sketch, "E577", {"start": v(-29.64, 4.82) * mm, "end": v(-29.88, 4.93) * mm});
            skLineSegment(sketch, "E578", {"start": v(-29.88, 4.93) * mm, "end": v(-30.11, 5.07) * mm});
            skLineSegment(sketch, "E579", {"start": v(-30.11, 5.07) * mm, "end": v(-30.35, 5.22) * mm});
            skLineSegment(sketch, "E580", {"start": v(-30.35, 5.22) * mm, "end": v(-30.58, 5.39) * mm});
            skLineSegment(sketch, "E581", {"start": v(-30.58, 5.39) * mm, "end": v(-30.8, 5.57) * mm});
            skLineSegment(sketch, "E582", {"start": v(-30.8, 5.57) * mm, "end": v(-31.02, 5.76) * mm});
            skLineSegment(sketch, "E583", {"start": v(-31.02, 5.76) * mm, "end": v(-31.24, 5.97) * mm});
            skLineSegment(sketch, "E584", {"start": v(-31.24, 5.97) * mm, "end": v(-31.45, 6.2) * mm});
            skLineSegment(sketch, "E585", {"start": v(-31.45, 6.2) * mm, "end": v(-31.61, 6.36) * mm});
            skLineSegment(sketch, "E586", {"start": v(-31.61, 6.36) * mm, "end": v(-30.89, 8.6) * mm});
            skLineSegment(sketch, "E587", {"start": v(-30.89, 8.6) * mm, "end": v(-30.66, 8.65) * mm});
            skLineSegment(sketch, "E588", {"start": v(-30.66, 8.65) * mm, "end": v(-30.36, 8.7) * mm});
            skLineSegment(sketch, "E589", {"start": v(-30.36, 8.7) * mm, "end": v(-30.06, 8.74) * mm});
            skLineSegment(sketch, "E590", {"start": v(-30.06, 8.74) * mm, "end": v(-29.77, 8.77) * mm});
            skLineSegment(sketch, "E591", {"start": v(-29.77, 8.77) * mm, "end": v(-29.48, 8.78) * mm});
            skLineSegment(sketch, "E592", {"start": v(-29.48, 8.78) * mm, "end": v(-29.2, 8.78) * mm});
            skLineSegment(sketch, "E593", {"start": v(-29.2, 8.78) * mm, "end": v(-28.91, 8.77) * mm});
            skLineSegment(sketch, "E594", {"start": v(-28.91, 8.77) * mm, "end": v(-28.64, 8.74) * mm});
            skLineSegment(sketch, "E595", {"start": v(-28.64, 8.74) * mm, "end": v(-28.38, 8.7) * mm});
            skLineSegment(sketch, "E596", {"start": v(-28.38, 8.7) * mm, "end": v(-28.13, 8.62) * mm});
            skLineSegment(sketch, "E597", {"start": v(-28.13, 8.62) * mm, "end": v(-27.89, 8.53) * mm});
            skLineSegment(sketch, "E598", {"start": v(-27.89, 8.53) * mm, "end": v(-27.66, 8.42) * mm});
            skLineSegment(sketch, "E599", {"start": v(-27.66, 8.42) * mm, "end": v(-27.53, 8.38) * mm});
            skLineSegment(sketch, "E600", {"start": v(-27.53, 8.38) * mm, "end": v(-27.4, 8.35) * mm});
            skLineSegment(sketch, "E601", {"start": v(-27.4, 8.35) * mm, "end": v(-27.27, 8.32) * mm});
            skLineSegment(sketch, "E602", {"start": v(-27.27, 8.32) * mm, "end": v(-27.13, 8.31) * mm});
            skLineSegment(sketch, "E603", {"start": v(-27.13, 8.31) * mm, "end": v(-27.06, 8.32) * mm});
            skLineSegment(sketch, "E604", {"start": v(-27.06, 8.32) * mm, "end": v(-26.98, 8.33) * mm});
            skLineSegment(sketch, "E605", {"start": v(-26.98, 8.33) * mm, "end": v(-26.9, 8.35) * mm});
            skLineSegment(sketch, "E606", {"start": v(-26.9, 8.35) * mm, "end": v(-26.8, 8.39) * mm});
            skLineSegment(sketch, "E607", {"start": v(-26.8, 8.39) * mm, "end": v(-26.64, 8.54) * mm});
            skLineSegment(sketch, "E608", {"start": v(-26.64, 8.54) * mm, "end": v(-26.12, 9.32) * mm});
            skLineSegment(sketch, "E609", {"start": v(-26.12, 9.32) * mm, "end": v(-25.54, 10.05) * mm});
            skLineSegment(sketch, "E610", {"start": v(-25.54, 10.05) * mm, "end": v(-25.44, 10.25) * mm});
            skLineSegment(sketch, "E611", {"start": v(-25.44, 10.25) * mm, "end": v(-25.43, 10.36) * mm});
            skLineSegment(sketch, "E612", {"start": v(-25.43, 10.36) * mm, "end": v(-25.44, 10.45) * mm});
            skLineSegment(sketch, "E613", {"start": v(-25.44, 10.45) * mm, "end": v(-25.46, 10.52) * mm});
            skLineSegment(sketch, "E614", {"start": v(-25.46, 10.52) * mm, "end": v(-25.48, 10.6) * mm});
            skLineSegment(sketch, "E615", {"start": v(-25.48, 10.6) * mm, "end": v(-25.53, 10.72) * mm});
            skLineSegment(sketch, "E616", {"start": v(-25.53, 10.72) * mm, "end": v(-25.6, 10.84) * mm});
            skLineSegment(sketch, "E617", {"start": v(-25.6, 10.84) * mm, "end": v(-25.66, 10.95) * mm});
            skLineSegment(sketch, "E618", {"start": v(-25.66, 10.95) * mm, "end": v(-25.74, 11.06) * mm});
            skLineSegment(sketch, "E619", {"start": v(-25.74, 11.06) * mm, "end": v(-25.91, 11.25) * mm});
            skLineSegment(sketch, "E620", {"start": v(-25.91, 11.25) * mm, "end": v(-26.08, 11.44) * mm});
            skLineSegment(sketch, "E621", {"start": v(-26.08, 11.44) * mm, "end": v(-26.22, 11.66) * mm});
            skLineSegment(sketch, "E622", {"start": v(-26.22, 11.66) * mm, "end": v(-26.35, 11.9) * mm});
            skLineSegment(sketch, "E623", {"start": v(-26.35, 11.9) * mm, "end": v(-26.46, 12.15) * mm});
            skLineSegment(sketch, "E624", {"start": v(-26.46, 12.15) * mm, "end": v(-26.56, 12.4) * mm});
            skLineSegment(sketch, "E625", {"start": v(-26.56, 12.4) * mm, "end": v(-26.64, 12.68) * mm});
            skLineSegment(sketch, "E626", {"start": v(-26.64, 12.68) * mm, "end": v(-26.72, 12.96) * mm});
            skLineSegment(sketch, "E627", {"start": v(-26.72, 12.96) * mm, "end": v(-26.78, 13.24) * mm});
            skLineSegment(sketch, "E628", {"start": v(-26.78, 13.24) * mm, "end": v(-26.84, 13.54) * mm});
            skLineSegment(sketch, "E629", {"start": v(-26.84, 13.54) * mm, "end": v(-26.88, 13.84) * mm});
            skLineSegment(sketch, "E630", {"start": v(-26.88, 13.84) * mm, "end": v(-26.9, 14.07) * mm});
            skLineSegment(sketch, "E631", {"start": v(-26.9, 14.07) * mm, "end": v(-25, 15.46) * mm});
            skLineSegment(sketch, "E632", {"start": v(-25, 15.46) * mm, "end": v(-24.8, 15.36) * mm});
            skLineSegment(sketch, "E633", {"start": v(-24.8, 15.36) * mm, "end": v(-24.52, 15.23) * mm});
            skLineSegment(sketch, "E634", {"start": v(-24.52, 15.23) * mm, "end": v(-24.25, 15.08) * mm});
            skLineSegment(sketch, "E635", {"start": v(-24.25, 15.08) * mm, "end": v(-24, 14.93) * mm});
            skLineSegment(sketch, "E636", {"start": v(-24, 14.93) * mm, "end": v(-23.76, 14.77) * mm});
            skLineSegment(sketch, "E637", {"start": v(-23.76, 14.77) * mm, "end": v(-23.53, 14.6) * mm});
            skLineSegment(sketch, "E638", {"start": v(-23.53, 14.6) * mm, "end": v(-23.31, 14.43) * mm});
            skLineSegment(sketch, "E639", {"start": v(-23.31, 14.43) * mm, "end": v(-23.11, 14.25) * mm});
            skLineSegment(sketch, "E640", {"start": v(-23.11, 14.25) * mm, "end": v(-22.92, 14.06) * mm});
            skLineSegment(sketch, "E641", {"start": v(-22.92, 14.06) * mm, "end": v(-22.76, 13.85) * mm});
            skLineSegment(sketch, "E642", {"start": v(-22.76, 13.85) * mm, "end": v(-22.62, 13.64) * mm});
            skLineSegment(sketch, "E643", {"start": v(-22.62, 13.64) * mm, "end": v(-22.5, 13.41) * mm});
            skLineSegment(sketch, "E644", {"start": v(-22.5, 13.41) * mm, "end": v(-22.42, 13.3) * mm});
            skLineSegment(sketch, "E645", {"start": v(-22.42, 13.3) * mm, "end": v(-22.34, 13.2) * mm});
            skLineSegment(sketch, "E646", {"start": v(-22.34, 13.2) * mm, "end": v(-22.25, 13.11) * mm});
            skLineSegment(sketch, "E647", {"start": v(-22.25, 13.11) * mm, "end": v(-22.14, 13.02) * mm});
            skLineSegment(sketch, "E648", {"start": v(-22.14, 13.02) * mm, "end": v(-22.08, 12.98) * mm});
            skLineSegment(sketch, "E649", {"start": v(-22.08, 12.98) * mm, "end": v(-22, 12.94) * mm});
            skLineSegment(sketch, "E650", {"start": v(-22, 12.94) * mm, "end": v(-21.93, 12.9) * mm});
            skLineSegment(sketch, "E651", {"start": v(-21.93, 12.9) * mm, "end": v(-21.83, 12.88) * mm});
            skLineSegment(sketch, "E652", {"start": v(-21.83, 12.88) * mm, "end": v(-21.6, 12.9) * mm});
            skLineSegment(sketch, "E653", {"start": v(-21.6, 12.9) * mm, "end": v(-20.73, 13.24) * mm});
            skLineSegment(sketch, "E654", {"start": v(-20.73, 13.24) * mm, "end": v(-19.82, 13.49) * mm});
            skLineSegment(sketch, "E655", {"start": v(-19.82, 13.49) * mm, "end": v(-19.63, 13.6) * mm});
            skLineSegment(sketch, "E656", {"start": v(-19.63, 13.6) * mm, "end": v(-19.56, 13.68) * mm});
            skLineSegment(sketch, "E657", {"start": v(-19.56, 13.68) * mm, "end": v(-19.52, 13.75) * mm});
            skLineSegment(sketch, "E658", {"start": v(-19.52, 13.75) * mm, "end": v(-19.48, 13.82) * mm});
            skLineSegment(sketch, "E659", {"start": v(-19.48, 13.82) * mm, "end": v(-19.46, 13.9) * mm});
            skLineSegment(sketch, "E660", {"start": v(-19.46, 13.9) * mm, "end": v(-19.42, 14.03) * mm});
            skLineSegment(sketch, "E661", {"start": v(-19.42, 14.03) * mm, "end": v(-19.4, 14.16) * mm});
            skLineSegment(sketch, "E662", {"start": v(-19.4, 14.16) * mm, "end": v(-19.4, 14.3) * mm});
            skLineSegment(sketch, "E663", {"start": v(-19.4, 14.3) * mm, "end": v(-19.4, 14.42) * mm});
            skLineSegment(sketch, "E664", {"start": v(-19.4, 14.42) * mm, "end": v(-19.43, 14.68) * mm});
            skLineSegment(sketch, "E665", {"start": v(-19.43, 14.68) * mm, "end": v(-19.45, 14.93) * mm});
            skLineSegment(sketch, "E666", {"start": v(-19.45, 14.93) * mm, "end": v(-19.43, 15.2) * mm});
            skLineSegment(sketch, "E667", {"start": v(-19.43, 15.2) * mm, "end": v(-19.4, 15.46) * mm});
            skLineSegment(sketch, "E668", {"start": v(-19.4, 15.46) * mm, "end": v(-19.34, 15.72) * mm});
            skLineSegment(sketch, "E669", {"start": v(-19.34, 15.72) * mm, "end": v(-19.26, 16) * mm});
            skLineSegment(sketch, "E670", {"start": v(-19.26, 16) * mm, "end": v(-19.18, 16.26) * mm});
            skLineSegment(sketch, "E671", {"start": v(-19.18, 16.26) * mm, "end": v(-19.07, 16.53) * mm});
            skLineSegment(sketch, "E672", {"start": v(-19.07, 16.53) * mm, "end": v(-18.96, 16.8) * mm});
            skLineSegment(sketch, "E673", {"start": v(-18.96, 16.8) * mm, "end": v(-18.83, 17.07) * mm});
            skLineSegment(sketch, "E674", {"start": v(-18.83, 17.07) * mm, "end": v(-18.68, 17.34) * mm});
            skLineSegment(sketch, "E675", {"start": v(-18.68, 17.34) * mm, "end": v(-18.57, 17.55) * mm});
            skLineSegment(sketch, "E676", {"start": v(-18.57, 17.55) * mm, "end": v(-16.22, 17.55) * mm});
            skLineSegment(sketch, "E677", {"start": v(-16.22, 17.55) * mm, "end": v(-16.1, 17.34) * mm});
            skLineSegment(sketch, "E678", {"start": v(-16.1, 17.34) * mm, "end": v(-15.96, 17.07) * mm});
            skLineSegment(sketch, "E679", {"start": v(-15.96, 17.07) * mm, "end": v(-15.83, 16.8) * mm});
            skLineSegment(sketch, "E680", {"start": v(-15.83, 16.8) * mm, "end": v(-15.71, 16.53) * mm});
            skLineSegment(sketch, "E681", {"start": v(-15.71, 16.53) * mm, "end": v(-15.61, 16.26) * mm});
            skLineSegment(sketch, "E682", {"start": v(-15.61, 16.26) * mm, "end": v(-15.52, 16) * mm});
            skLineSegment(sketch, "E683", {"start": v(-15.52, 16) * mm, "end": v(-15.45, 15.72) * mm});
            skLineSegment(sketch, "E684", {"start": v(-15.45, 15.72) * mm, "end": v(-15.4, 15.46) * mm});
            skLineSegment(sketch, "E685", {"start": v(-15.4, 15.46) * mm, "end": v(-15.36, 15.2) * mm});
            skLineSegment(sketch, "E686", {"start": v(-15.36, 15.2) * mm, "end": v(-15.34, 14.93) * mm});
            skLineSegment(sketch, "E687", {"start": v(-15.34, 14.93) * mm, "end": v(-15.36, 14.68) * mm});
            skLineSegment(sketch, "E688", {"start": v(-15.36, 14.68) * mm, "end": v(-15.39, 14.42) * mm});
            skLineSegment(sketch, "E689", {"start": v(-15.39, 14.42) * mm, "end": v(-15.4, 14.3) * mm});
            skLineSegment(sketch, "E690", {"start": v(-15.4, 14.3) * mm, "end": v(-15.38, 14.16) * mm});
            skLineSegment(sketch, "E691", {"start": v(-15.38, 14.16) * mm, "end": v(-15.37, 14.03) * mm});
            skLineSegment(sketch, "E692", {"start": v(-15.37, 14.03) * mm, "end": v(-15.33, 13.9) * mm});
            skLineSegment(sketch, "E693", {"start": v(-15.33, 13.9) * mm, "end": v(-15.3, 13.82) * mm});
            skLineSegment(sketch, "E694", {"start": v(-15.3, 13.82) * mm, "end": v(-15.27, 13.75) * mm});
            skLineSegment(sketch, "E695", {"start": v(-15.27, 13.75) * mm, "end": v(-15.23, 13.68) * mm});
            skLineSegment(sketch, "E696", {"start": v(-15.23, 13.68) * mm, "end": v(-15.16, 13.6) * mm});
            skLineSegment(sketch, "E697", {"start": v(-15.16, 13.6) * mm, "end": v(-14.97, 13.49) * mm});
            skLineSegment(sketch, "E698", {"start": v(-14.97, 13.49) * mm, "end": v(-14.06, 13.24) * mm});
            skLineSegment(sketch, "E699", {"start": v(-14.06, 13.24) * mm, "end": v(-13.18, 12.9) * mm});
            skLineSegment(sketch, "E700", {"start": v(-13.18, 12.9) * mm, "end": v(-12.96, 12.88) * mm});
            skLineSegment(sketch, "E701", {"start": v(-12.96, 12.88) * mm, "end": v(-12.86, 12.9) * mm});
            skLineSegment(sketch, "E702", {"start": v(-12.86, 12.9) * mm, "end": v(-12.78, 12.94) * mm});
            skLineSegment(sketch, "E703", {"start": v(-12.78, 12.94) * mm, "end": v(-12.71, 12.98) * mm});
            skLineSegment(sketch, "E704", {"start": v(-12.71, 12.98) * mm, "end": v(-12.65, 13.02) * mm});
            skLineSegment(sketch, "E705", {"start": v(-12.65, 13.02) * mm, "end": v(-12.54, 13.11) * mm});
            skLineSegment(sketch, "E706", {"start": v(-12.54, 13.11) * mm, "end": v(-12.45, 13.2) * mm});
            skLineSegment(sketch, "E707", {"start": v(-12.45, 13.2) * mm, "end": v(-12.37, 13.3) * mm});
            skLineSegment(sketch, "E708", {"start": v(-12.37, 13.3) * mm, "end": v(-12.3, 13.41) * mm});
            skLineSegment(sketch, "E709", {"start": v(-12.3, 13.41) * mm, "end": v(-12.16, 13.64) * mm});
            skLineSegment(sketch, "E710", {"start": v(-12.16, 13.64) * mm, "end": v(-12.03, 13.85) * mm});
            skLineSegment(sketch, "E711", {"start": v(-12.03, 13.85) * mm, "end": v(-11.86, 14.06) * mm});
            skLineSegment(sketch, "E712", {"start": v(-11.86, 14.06) * mm, "end": v(-11.68, 14.25) * mm});
            skLineSegment(sketch, "E713", {"start": v(-11.68, 14.25) * mm, "end": v(-11.48, 14.43) * mm});
            skLineSegment(sketch, "E714", {"start": v(-11.48, 14.43) * mm, "end": v(-11.26, 14.6) * mm});
            skLineSegment(sketch, "E715", {"start": v(-11.26, 14.6) * mm, "end": v(-11.03, 14.77) * mm});
            skLineSegment(sketch, "E716", {"start": v(-11.03, 14.77) * mm, "end": v(-10.79, 14.93) * mm});
            skLineSegment(sketch, "E717", {"start": v(-10.79, 14.93) * mm, "end": v(-10.53, 15.08) * mm});
            skLineSegment(sketch, "E718", {"start": v(-10.53, 15.08) * mm, "end": v(-10.27, 15.23) * mm});
            skLineSegment(sketch, "E719", {"start": v(-10.27, 15.23) * mm, "end": v(-10, 15.36) * mm});
            skLineSegment(sketch, "E720", {"start": v(-10, 15.36) * mm, "end": v(-9.78, 15.46) * mm});
            skLineSegment(sketch, "E721", {"start": v(-9.78, 15.46) * mm, "end": v(-7.88, 14.07) * mm});
            skLineSegment(sketch, "E722", {"start": v(-7.88, 14.07) * mm, "end": v(-7.9, 13.84) * mm});
            skLineSegment(sketch, "E723", {"start": v(-7.9, 13.84) * mm, "end": v(-7.95, 13.54) * mm});
            skLineSegment(sketch, "E724", {"start": v(-7.95, 13.54) * mm, "end": v(-8, 13.24) * mm});
            skLineSegment(sketch, "E725", {"start": v(-8, 13.24) * mm, "end": v(-8.07, 12.96) * mm});
            skLineSegment(sketch, "E726", {"start": v(-8.07, 12.96) * mm, "end": v(-8.14, 12.68) * mm});
            skLineSegment(sketch, "E727", {"start": v(-8.14, 12.68) * mm, "end": v(-8.23, 12.4) * mm});
            skLineSegment(sketch, "E728", {"start": v(-8.23, 12.4) * mm, "end": v(-8.33, 12.15) * mm});
            skLineSegment(sketch, "E729", {"start": v(-8.33, 12.15) * mm, "end": v(-8.44, 11.9) * mm});
            skLineSegment(sketch, "E730", {"start": v(-8.44, 11.9) * mm, "end": v(-8.57, 11.66) * mm});
            skLineSegment(sketch, "E731", {"start": v(-8.57, 11.66) * mm, "end": v(-8.7, 11.44) * mm});
            skLineSegment(sketch, "E732", {"start": v(-8.7, 11.44) * mm, "end": v(-8.88, 11.25) * mm});
            skLineSegment(sketch, "E733", {"start": v(-8.88, 11.25) * mm, "end": v(-9.05, 11.06) * mm});
            skLineSegment(sketch, "E734", {"start": v(-9.05, 11.06) * mm, "end": v(-9.12, 10.95) * mm});
            skLineSegment(sketch, "E735", {"start": v(-9.12, 10.95) * mm, "end": v(-9.2, 10.84) * mm});
            skLineSegment(sketch, "E736", {"start": v(-9.2, 10.84) * mm, "end": v(-9.26, 10.72) * mm});
            skLineSegment(sketch, "E737", {"start": v(-9.26, 10.72) * mm, "end": v(-9.31, 10.6) * mm});
            skLineSegment(sketch, "E738", {"start": v(-9.31, 10.6) * mm, "end": v(-9.33, 10.52) * mm});
            skLineSegment(sketch, "E739", {"start": v(-9.33, 10.52) * mm, "end": v(-9.35, 10.45) * mm});
            skLineSegment(sketch, "E740", {"start": v(-9.35, 10.45) * mm, "end": v(-9.35, 10.36) * mm});
            skLineSegment(sketch, "E741", {"start": v(-9.35, 10.36) * mm, "end": v(-9.35, 10.25) * mm});
            skLineSegment(sketch, "E742", {"start": v(-9.35, 10.25) * mm, "end": v(-9.25, 10.05) * mm});
            skLineSegment(sketch, "E743", {"start": v(-9.25, 10.05) * mm, "end": v(-8.67, 9.32) * mm});
            skLineSegment(sketch, "E744", {"start": v(-8.67, 9.32) * mm, "end": v(-8.15, 8.54) * mm});
            skLineSegment(sketch, "E745", {"start": v(-8.15, 8.54) * mm, "end": v(-7.99, 8.39) * mm});
            skLineSegment(sketch, "E746", {"start": v(-7.99, 8.39) * mm, "end": v(-7.9, 8.35) * mm});
            skLineSegment(sketch, "E747", {"start": v(-7.9, 8.35) * mm, "end": v(-7.8, 8.33) * mm});
            skLineSegment(sketch, "E748", {"start": v(-7.8, 8.33) * mm, "end": v(-7.73, 8.32) * mm});
            skLineSegment(sketch, "E749", {"start": v(-7.73, 8.32) * mm, "end": v(-7.65, 8.31) * mm});
            skLineSegment(sketch, "E750", {"start": v(-7.65, 8.31) * mm, "end": v(-7.51, 8.32) * mm});
            skLineSegment(sketch, "E751", {"start": v(-7.51, 8.32) * mm, "end": v(-7.38, 8.35) * mm});
            skLineSegment(sketch, "E752", {"start": v(-7.38, 8.35) * mm, "end": v(-7.26, 8.38) * mm});
            skLineSegment(sketch, "E753", {"start": v(-7.26, 8.38) * mm, "end": v(-7.13, 8.42) * mm});
            skLineSegment(sketch, "E754", {"start": v(-7.13, 8.42) * mm, "end": v(-6.9, 8.53) * mm});
            skLineSegment(sketch, "E755", {"start": v(-6.9, 8.53) * mm, "end": v(-6.66, 8.62) * mm});
            skLineSegment(sketch, "E756", {"start": v(-6.66, 8.62) * mm, "end": v(-6.4, 8.7) * mm});
            skLineSegment(sketch, "E757", {"start": v(-6.4, 8.7) * mm, "end": v(-6.15, 8.74) * mm});
            skLineSegment(sketch, "E758", {"start": v(-6.15, 8.74) * mm, "end": v(-5.87, 8.77) * mm});
            skLineSegment(sketch, "E759", {"start": v(-5.87, 8.77) * mm, "end": v(-5.6, 8.78) * mm});
            skLineSegment(sketch, "E760", {"start": v(-5.6, 8.78) * mm, "end": v(-5.31, 8.78) * mm});
            skLineSegment(sketch, "E761", {"start": v(-5.31, 8.78) * mm, "end": v(-5.02, 8.77) * mm});
            skLineSegment(sketch, "E762", {"start": v(-5.02, 8.77) * mm, "end": v(-4.73, 8.74) * mm});
            skLineSegment(sketch, "E763", {"start": v(-4.73, 8.74) * mm, "end": v(-4.43, 8.7) * mm});
            skLineSegment(sketch, "E764", {"start": v(-4.43, 8.7) * mm, "end": v(-4.13, 8.65) * mm});
            skLineSegment(sketch, "E765", {"start": v(-4.13, 8.65) * mm, "end": v(-3.9, 8.6) * mm});
            skLineSegment(sketch, "E766", {"start": v(-3.9, 8.6) * mm, "end": v(-3.18, 6.36) * mm});
            skLineSegment(sketch, "E767", {"start": v(-3.18, 6.36) * mm, "end": v(-3.33, 6.2) * mm});
            skLineSegment(sketch, "E768", {"start": v(-3.33, 6.2) * mm, "end": v(-3.55, 5.97) * mm});
            skLineSegment(sketch, "E769", {"start": v(-3.55, 5.97) * mm, "end": v(-3.76, 5.76) * mm});
            skLineSegment(sketch, "E770", {"start": v(-3.76, 5.76) * mm, "end": v(-3.98, 5.57) * mm});
            skLineSegment(sketch, "E771", {"start": v(-3.98, 5.57) * mm, "end": v(-4.21, 5.39) * mm});
            skLineSegment(sketch, "E772", {"start": v(-4.21, 5.39) * mm, "end": v(-4.44, 5.22) * mm});
            skLineSegment(sketch, "E773", {"start": v(-4.44, 5.22) * mm, "end": v(-4.67, 5.07) * mm});
            skLineSegment(sketch, "E774", {"start": v(-4.67, 5.07) * mm, "end": v(-4.9, 4.93) * mm});
            skLineSegment(sketch, "E775", {"start": v(-4.9, 4.93) * mm, "end": v(-5.15, 4.82) * mm});
            skLineSegment(sketch, "E776", {"start": v(-5.15, 4.82) * mm, "end": v(-5.4, 4.72) * mm});
            skLineSegment(sketch, "E777", {"start": v(-5.4, 4.72) * mm, "end": v(-5.64, 4.66) * mm});
            skLineSegment(sketch, "E778", {"start": v(-5.64, 4.66) * mm, "end": v(-5.9, 4.6) * mm});
            skLineSegment(sketch, "E779", {"start": v(-5.9, 4.6) * mm, "end": v(-6.02, 4.57) * mm});
            skLineSegment(sketch, "E780", {"start": v(-6.02, 4.57) * mm, "end": v(-6.14, 4.52) * mm});
            skLineSegment(sketch, "E781", {"start": v(-6.14, 4.52) * mm, "end": v(-6.26, 4.46) * mm});
            skLineSegment(sketch, "E782", {"start": v(-6.26, 4.46) * mm, "end": v(-6.38, 4.39) * mm});
            skLineSegment(sketch, "E783", {"start": v(-6.38, 4.39) * mm, "end": v(-6.44, 4.34) * mm});
            skLineSegment(sketch, "E784", {"start": v(-6.44, 4.34) * mm, "end": v(-6.5, 4.29) * mm});
            skLineSegment(sketch, "E785", {"start": v(-6.5, 4.29) * mm, "end": v(-6.55, 4.22) * mm});
            skLineSegment(sketch, "E786", {"start": v(-6.55, 4.22) * mm, "end": v(-6.6, 4.13) * mm});
            skLineSegment(sketch, "E787", {"start": v(-6.6, 4.13) * mm, "end": v(-6.65, 3.92) * mm});
            skLineSegment(sketch, "E788", {"start": v(-6.65, 3.92) * mm, "end": v(-6.6, 2.98) * mm});
            skLineSegment(sketch, "E789", {"start": v(-6.6, 2.98) * mm, "end": v(-6.65, 2.04) * mm});
            skLineSegment(sketch, "E790", {"start": v(-6.65, 2.04) * mm, "end": v(-6.6, 1.83) * mm});
            skLineSegment(sketch, "E791", {"start": v(-6.6, 1.83) * mm, "end": v(-6.55, 1.74) * mm});
            skLineSegment(sketch, "E792", {"start": v(-6.55, 1.74) * mm, "end": v(-6.5, 1.67) * mm});
            skLineSegment(sketch, "E793", {"start": v(-6.5, 1.67) * mm, "end": v(-6.44, 1.62) * mm});
            skLineSegment(sketch, "E794", {"start": v(-6.44, 1.62) * mm, "end": v(-6.38, 1.57) * mm});
            skLineSegment(sketch, "E795", {"start": v(-6.38, 1.57) * mm, "end": v(-6.26, 1.5) * mm});
            skLineSegment(sketch, "E796", {"start": v(-6.26, 1.5) * mm, "end": v(-6.14, 1.44) * mm});
            skLineSegment(sketch, "E797", {"start": v(-6.14, 1.44) * mm, "end": v(-6.02, 1.39) * mm});
            skLineSegment(sketch, "E798", {"start": v(-6.02, 1.39) * mm, "end": v(-5.9, 1.35) * mm});
            skLineSegment(sketch, "E799", {"start": v(-5.9, 1.35) * mm, "end": v(-5.64, 1.3) * mm});
            skLineSegment(sketch, "E800", {"start": v(-5.64, 1.3) * mm, "end": v(-5.4, 1.24) * mm});
            skLineSegment(sketch, "E801", {"start": v(-5.4, 1.24) * mm, "end": v(-5.15, 1.14) * mm});
            skLineSegment(sketch, "E802", {"start": v(-5.15, 1.14) * mm, "end": v(-4.9, 1.03) * mm});
            skLineSegment(sketch, "E803", {"start": v(-4.9, 1.03) * mm, "end": v(-4.67, 0.89) * mm});
            skLineSegment(sketch, "E804", {"start": v(-4.67, 0.89) * mm, "end": v(-4.44, 0.74) * mm});
            skLineSegment(sketch, "E805", {"start": v(-4.44, 0.74) * mm, "end": v(-4.21, 0.57) * mm});
            skLineSegment(sketch, "E806", {"start": v(-4.21, 0.57) * mm, "end": v(-3.98, 0.39) * mm});
            skLineSegment(sketch, "E807", {"start": v(-3.98, 0.39) * mm, "end": v(-3.76, 0.2) * mm});
            skLineSegment(sketch, "E808", {"start": v(-3.76, 0.2) * mm, "end": v(-3.55, -0.01) * mm});
            skLineSegment(sketch, "E809", {"start": v(-3.55, -0.01) * mm, "end": v(-3.33, -0.23) * mm});
            skLineSegment(sketch, "E810", {"start": v(-3.33, -0.23) * mm, "end": v(-3.18, -0.4) * mm});
            skLineSegment(sketch, "E811", {"start": v(-3.18, -0.4) * mm, "end": v(-3.9, -2.64) * mm});
            skLineSegment(sketch, "E812", {"start": v(-3.9, -2.64) * mm, "end": v(-4.13, -2.69) * mm});
            skLineSegment(sketch, "E813", {"start": v(-4.13, -2.69) * mm, "end": v(-4.43, -2.74) * mm});
            skLineSegment(sketch, "E814", {"start": v(-4.43, -2.74) * mm, "end": v(-4.73, -2.78) * mm});
            skLineSegment(sketch, "E815", {"start": v(-4.73, -2.78) * mm, "end": v(-5.02, -2.8) * mm});
            skLineSegment(sketch, "E816", {"start": v(-5.02, -2.8) * mm, "end": v(-5.31, -2.82) * mm});
            skLineSegment(sketch, "E817", {"start": v(-5.31, -2.82) * mm, "end": v(-5.6, -2.82) * mm});
            skLineSegment(sketch, "E818", {"start": v(-5.6, -2.82) * mm, "end": v(-5.87, -2.8) * mm});
            skLineSegment(sketch, "E819", {"start": v(-5.87, -2.8) * mm, "end": v(-6.15, -2.78) * mm});
            skLineSegment(sketch, "E820", {"start": v(-6.15, -2.78) * mm, "end": v(-6.4, -2.73) * mm});
            skLineSegment(sketch, "E821", {"start": v(-6.4, -2.73) * mm, "end": v(-6.66, -2.67) * mm});
            skLineSegment(sketch, "E822", {"start": v(-6.66, -2.67) * mm, "end": v(-6.9, -2.57) * mm});
            skLineSegment(sketch, "E823", {"start": v(-6.9, -2.57) * mm, "end": v(-7.13, -2.46) * mm});
            skLineSegment(sketch, "E824", {"start": v(-7.13, -2.46) * mm, "end": v(-7.26, -2.42) * mm});
            skLineSegment(sketch, "E825", {"start": v(-7.26, -2.42) * mm, "end": v(-7.38, -2.39) * mm});
            skLineSegment(sketch, "E826", {"start": v(-7.38, -2.39) * mm, "end": v(-7.51, -2.36) * mm});
            skLineSegment(sketch, "E827", {"start": v(-7.51, -2.36) * mm, "end": v(-7.65, -2.35) * mm});
            skLineSegment(sketch, "E828", {"start": v(-7.65, -2.35) * mm, "end": v(-7.73, -2.36) * mm});
            skLineSegment(sketch, "E829", {"start": v(-7.73, -2.36) * mm, "end": v(-7.8, -2.37) * mm});
            skLineSegment(sketch, "E830", {"start": v(-7.8, -2.37) * mm, "end": v(-7.9, -2.39) * mm});
            skLineSegment(sketch, "E831", {"start": v(-7.9, -2.39) * mm, "end": v(-7.99, -2.43) * mm});
            skLineSegment(sketch, "E832", {"start": v(-7.99, -2.43) * mm, "end": v(-8.15, -2.58) * mm});
            skLineSegment(sketch, "E833", {"start": v(-8.15, -2.58) * mm, "end": v(-8.67, -3.36) * mm});
            skLineSegment(sketch, "E834", {"start": v(-8.67, -3.36) * mm, "end": v(-9.25, -4.1) * mm});
            skLineSegment(sketch, "E835", {"start": v(-9.25, -4.1) * mm, "end": v(-9.35, -4.3) * mm});
            skLineSegment(sketch, "E836", {"start": v(-9.35, -4.3) * mm, "end": v(-9.35, -4.4) * mm});
            skLineSegment(sketch, "E837", {"start": v(-9.35, -4.4) * mm, "end": v(-9.35, -4.49) * mm});
            skLineSegment(sketch, "E838", {"start": v(-9.35, -4.49) * mm, "end": v(-9.33, -4.56) * mm});
            skLineSegment(sketch, "E839", {"start": v(-9.33, -4.56) * mm, "end": v(-9.31, -4.63) * mm});
            skLineSegment(sketch, "E840", {"start": v(-9.31, -4.63) * mm, "end": v(-9.26, -4.77) * mm});
            skLineSegment(sketch, "E841", {"start": v(-9.26, -4.77) * mm, "end": v(-9.2, -4.88) * mm});
            skLineSegment(sketch, "E842", {"start": v(-9.2, -4.88) * mm, "end": v(-9.12, -5) * mm});
            skLineSegment(sketch, "E843", {"start": v(-9.12, -5) * mm, "end": v(-9.05, -5.1) * mm});
            skLineSegment(sketch, "E844", {"start": v(-9.05, -5.1) * mm, "end": v(-8.88, -5.29) * mm});
            skLineSegment(sketch, "E845", {"start": v(-8.88, -5.29) * mm, "end": v(-8.7, -5.48) * mm});
            skLineSegment(sketch, "E846", {"start": v(-8.7, -5.48) * mm, "end": v(-8.57, -5.7) * mm});
            skLineSegment(sketch, "E847", {"start": v(-8.57, -5.7) * mm, "end": v(-8.44, -5.94) * mm});
            skLineSegment(sketch, "E848", {"start": v(-8.44, -5.94) * mm, "end": v(-8.33, -6.19) * mm});
            skLineSegment(sketch, "E849", {"start": v(-8.33, -6.19) * mm, "end": v(-8.23, -6.45) * mm});
            skLineSegment(sketch, "E850", {"start": v(-8.23, -6.45) * mm, "end": v(-8.14, -6.72) * mm});
            skLineSegment(sketch, "E851", {"start": v(-8.14, -6.72) * mm, "end": v(-8.07, -7) * mm});
            skLineSegment(sketch, "E852", {"start": v(-8.07, -7) * mm, "end": v(-8, -7.29) * mm});
            skLineSegment(sketch, "E853", {"start": v(-8, -7.29) * mm, "end": v(-7.95, -7.58) * mm});
            skLineSegment(sketch, "E854", {"start": v(-7.95, -7.58) * mm, "end": v(-7.9, -7.88) * mm});
            skLineSegment(sketch, "E855", {"start": v(-7.9, -7.88) * mm, "end": v(-7.88, -8.11) * mm});
            skLineSegment(sketch, "E856", {"start": v(-7.88, -8.11) * mm, "end": v(-9.78, -9.5) * mm});
            skLineSegment(sketch, "E857", {"start": v(-9.78, -9.5) * mm, "end": v(-10, -9.4) * mm});
            skLineSegment(sketch, "E858", {"start": v(-10, -9.4) * mm, "end": v(-10.27, -9.27) * mm});
            skLineSegment(sketch, "E859", {"start": v(-10.27, -9.27) * mm, "end": v(-10.53, -9.12) * mm});
            skLineSegment(sketch, "E860", {"start": v(-10.53, -9.12) * mm, "end": v(-10.79, -8.97) * mm});
            skLineSegment(sketch, "E861", {"start": v(-10.79, -8.97) * mm, "end": v(-11.03, -8.81) * mm});
            skLineSegment(sketch, "E862", {"start": v(-11.03, -8.81) * mm, "end": v(-11.26, -8.65) * mm});
            skLineSegment(sketch, "E863", {"start": v(-11.26, -8.65) * mm, "end": v(-11.48, -8.47) * mm});
            skLineSegment(sketch, "E864", {"start": v(-11.48, -8.47) * mm, "end": v(-11.68, -8.29) * mm});
            skLineSegment(sketch, "E865", {"start": v(-11.68, -8.29) * mm, "end": v(-11.86, -8.1) * mm});
            skLineSegment(sketch, "E866", {"start": v(-11.86, -8.1) * mm, "end": v(-12.03, -7.9) * mm});
            skLineSegment(sketch, "E867", {"start": v(-12.03, -7.9) * mm, "end": v(-12.16, -7.68) * mm});
            skLineSegment(sketch, "E868", {"start": v(-12.16, -7.68) * mm, "end": v(-12.3, -7.45) * mm});
            skLineSegment(sketch, "E869", {"start": v(-12.3, -7.45) * mm, "end": v(-12.37, -7.35) * mm});
            skLineSegment(sketch, "E870", {"start": v(-12.37, -7.35) * mm, "end": v(-12.45, -7.25) * mm});
            skLineSegment(sketch, "E871", {"start": v(-12.45, -7.25) * mm, "end": v(-12.54, -7.15) * mm});
            skLineSegment(sketch, "E872", {"start": v(-12.54, -7.15) * mm, "end": v(-12.65, -7.06) * mm});
            skLineSegment(sketch, "E873", {"start": v(-12.65, -7.06) * mm, "end": v(-12.71, -7.02) * mm});
            skLineSegment(sketch, "E874", {"start": v(-12.71, -7.02) * mm, "end": v(-12.78, -6.98) * mm});
            skLineSegment(sketch, "E875", {"start": v(-12.78, -6.98) * mm, "end": v(-12.86, -6.95) * mm});
            skLineSegment(sketch, "E876", {"start": v(-12.86, -6.95) * mm, "end": v(-12.96, -6.92) * mm});
            skLineSegment(sketch, "E877", {"start": v(-12.96, -6.92) * mm, "end": v(-13.18, -6.95) * mm});
            skLineSegment(sketch, "E878", {"start": v(-13.18, -6.95) * mm, "end": v(-14.06, -7.28) * mm});
            skLineSegment(sketch, "E879", {"start": v(-14.06, -7.28) * mm, "end": v(-14.97, -7.53) * mm});
            skLineSegment(sketch, "E880", {"start": v(-14.97, -7.53) * mm, "end": v(-15.16, -7.64) * mm});
            skLineSegment(sketch, "E881", {"start": v(-15.16, -7.64) * mm, "end": v(-15.23, -7.72) * mm});
            skLineSegment(sketch, "E882", {"start": v(-15.23, -7.72) * mm, "end": v(-15.27, -7.8) * mm});
            skLineSegment(sketch, "E883", {"start": v(-15.27, -7.8) * mm, "end": v(-15.3, -7.86) * mm});
            skLineSegment(sketch, "E884", {"start": v(-15.3, -7.86) * mm, "end": v(-15.33, -7.93) * mm});
            skLineSegment(sketch, "E885", {"start": v(-15.33, -7.93) * mm, "end": v(-15.37, -8.07) * mm});
            skLineSegment(sketch, "E886", {"start": v(-15.37, -8.07) * mm, "end": v(-15.38, -8.2) * mm});
            skLineSegment(sketch, "E887", {"start": v(-15.38, -8.2) * mm, "end": v(-15.4, -8.33) * mm});
            skLineSegment(sketch, "E888", {"start": v(-15.4, -8.33) * mm, "end": v(-15.39, -8.46) * mm});
            skLineSegment(sketch, "E889", {"start": v(-15.39, -8.46) * mm, "end": v(-15.36, -8.72) * mm});
            skLineSegment(sketch, "E890", {"start": v(-15.36, -8.72) * mm, "end": v(-15.34, -8.97) * mm});
            skLineSegment(sketch, "E891", {"start": v(-15.34, -8.97) * mm, "end": v(-15.36, -9.23) * mm});
            skLineSegment(sketch, "E892", {"start": v(-15.36, -9.23) * mm, "end": v(-15.4, -9.5) * mm});
            skLineSegment(sketch, "E893", {"start": v(-15.4, -9.5) * mm, "end": v(-15.45, -9.76) * mm});
            skLineSegment(sketch, "E894", {"start": v(-15.45, -9.76) * mm, "end": v(-15.52, -10.03) * mm});
            skLineSegment(sketch, "E895", {"start": v(-15.52, -10.03) * mm, "end": v(-15.61, -10.3) * mm});
            skLineSegment(sketch, "E896", {"start": v(-15.61, -10.3) * mm, "end": v(-15.71, -10.57) * mm});
            skLineSegment(sketch, "E897", {"start": v(-15.71, -10.57) * mm, "end": v(-15.83, -10.84) * mm});
            skLineSegment(sketch, "E898", {"start": v(-15.83, -10.84) * mm, "end": v(-15.96, -11.12) * mm});
            skLineSegment(sketch, "E899", {"start": v(-15.96, -11.12) * mm, "end": v(-16.1, -11.39) * mm});
            skLineSegment(sketch, "E900", {"start": v(-16.1, -11.39) * mm, "end": v(-16.22, -11.59) * mm});
            skLineSegment(sketch, "E901", {"start": v(-16.22, -11.59) * mm, "end": v(-18.57, -11.59) * mm});
            skLineSegment(sketch, "E902", {"start": v(-18.57, -11.59) * mm, "end": v(-18.68, -11.39) * mm});
            skLineSegment(sketch, "E903", {"start": v(-18.68, -11.39) * mm, "end": v(-18.83, -11.12) * mm});
            skLineSegment(sketch, "E904", {"start": v(-18.83, -11.12) * mm, "end": v(-18.96, -10.84) * mm});
            skLineSegment(sketch, "E905", {"start": v(-18.96, -10.84) * mm, "end": v(-19.07, -10.57) * mm});
            skLineSegment(sketch, "E906", {"start": v(-19.07, -10.57) * mm, "end": v(-19.18, -10.3) * mm});
            skLineSegment(sketch, "E907", {"start": v(-19.18, -10.3) * mm, "end": v(-19.26, -10.03) * mm});
            skLineSegment(sketch, "E908", {"start": v(-19.26, -10.03) * mm, "end": v(-19.34, -9.76) * mm});
            skLineSegment(sketch, "E909", {"start": v(-19.34, -9.76) * mm, "end": v(-19.4, -9.5) * mm});
            skLineSegment(sketch, "E910", {"start": v(-19.4, -9.5) * mm, "end": v(-19.43, -9.23) * mm});
            skLineSegment(sketch, "E911", {"start": v(-19.43, -9.23) * mm, "end": v(-19.45, -8.97) * mm});
            skLineSegment(sketch, "E912", {"start": v(-19.45, -8.97) * mm, "end": v(-19.43, -8.72) * mm});
            skLineSegment(sketch, "E913", {"start": v(-19.43, -8.72) * mm, "end": v(-19.4, -8.46) * mm});
            skLineSegment(sketch, "E914", {"start": v(-19.4, -8.46) * mm, "end": v(-19.4, -8.33) * mm});
            skLineSegment(sketch, "E915", {"start": v(-19.4, -8.33) * mm, "end": v(-19.4, -8.2) * mm});
            skLineSegment(sketch, "E916", {"start": v(-19.4, -8.2) * mm, "end": v(-19.42, -8.07) * mm});
            skLineSegment(sketch, "E917", {"start": v(-19.42, -8.07) * mm, "end": v(-19.46, -7.93) * mm});
            skLineSegment(sketch, "E918", {"start": v(-19.46, -7.93) * mm, "end": v(-19.48, -7.86) * mm});
            skLineSegment(sketch, "E919", {"start": v(-19.48, -7.86) * mm, "end": v(-19.52, -7.8) * mm});
            skLineSegment(sketch, "E920", {"start": v(-19.52, -7.8) * mm, "end": v(-19.56, -7.72) * mm});
            skLineSegment(sketch, "E921", {"start": v(-19.56, -7.72) * mm, "end": v(-19.63, -7.64) * mm});
            skLineSegment(sketch, "E922", {"start": v(-19.63, -7.64) * mm, "end": v(-19.82, -7.53) * mm});
            skLineSegment(sketch, "E923", {"start": v(-19.82, -7.53) * mm, "end": v(-20.73, -7.28) * mm});
            skLineSegment(sketch, "E924", {"start": v(-20.73, -7.28) * mm, "end": v(-21.6, -6.95) * mm});
            skLineSegment(sketch, "E925", {"start": v(-21.6, -6.95) * mm, "end": v(-21.83, -6.92) * mm});
            skLineSegment(sketch, "E926", {"start": v(-21.83, -6.92) * mm, "end": v(-21.93, -6.95) * mm});
            skLineSegment(sketch, "E927", {"start": v(-21.93, -6.95) * mm, "end": v(-22, -6.98) * mm});
            skLineSegment(sketch, "E928", {"start": v(-22, -6.98) * mm, "end": v(-22.08, -7.02) * mm});
            skLineSegment(sketch, "E929", {"start": v(-22.08, -7.02) * mm, "end": v(-22.14, -7.06) * mm});
            skLineSegment(sketch, "E930", {"start": v(-22.14, -7.06) * mm, "end": v(-22.25, -7.15) * mm});
            skLineSegment(sketch, "E931", {"start": v(-22.25, -7.15) * mm, "end": v(-22.34, -7.25) * mm});
            skLineSegment(sketch, "E932", {"start": v(-22.34, -7.25) * mm, "end": v(-22.42, -7.35) * mm});
            skLineSegment(sketch, "E933", {"start": v(-22.42, -7.35) * mm, "end": v(-22.5, -7.45) * mm});
            skLineSegment(sketch, "E934", {"start": v(-22.5, -7.45) * mm, "end": v(-22.62, -7.68) * mm});
            skLineSegment(sketch, "E935", {"start": v(-22.62, -7.68) * mm, "end": v(-22.76, -7.9) * mm});
            skLineSegment(sketch, "E936", {"start": v(-22.76, -7.9) * mm, "end": v(-22.92, -8.1) * mm});
            skLineSegment(sketch, "E937", {"start": v(-22.92, -8.1) * mm, "end": v(-23.11, -8.29) * mm});
            skLineSegment(sketch, "E938", {"start": v(-23.11, -8.29) * mm, "end": v(-23.31, -8.47) * mm});
            skLineSegment(sketch, "E939", {"start": v(-23.31, -8.47) * mm, "end": v(-23.53, -8.65) * mm});
            skLineSegment(sketch, "E940", {"start": v(-23.53, -8.65) * mm, "end": v(-23.76, -8.81) * mm});
            skLineSegment(sketch, "E941", {"start": v(-23.76, -8.81) * mm, "end": v(-24, -8.97) * mm});
            skLineSegment(sketch, "E942", {"start": v(-24, -8.97) * mm, "end": v(-24.25, -9.12) * mm});
            skLineSegment(sketch, "E943", {"start": v(-24.25, -9.12) * mm, "end": v(-24.52, -9.27) * mm});
            skLineSegment(sketch, "E944", {"start": v(-24.52, -9.27) * mm, "end": v(-24.8, -9.4) * mm});
            skLineSegment(sketch, "E945", {"start": v(-24.8, -9.4) * mm, "end": v(-25, -9.5) * mm});
            skLineSegment(sketch, "E946", {"start": v(-25, -9.5) * mm, "end": v(-26.9, -8.11) * mm});
            skLineSegment(sketch, "E947", {"start": v(-26.9, -8.11) * mm, "end": v(-26.88, -7.88) * mm});
            skLineSegment(sketch, "E948", {"start": v(-26.88, -7.88) * mm, "end": v(-26.84, -7.58) * mm});
            skLineSegment(sketch, "E949", {"start": v(-26.84, -7.58) * mm, "end": v(-26.78, -7.29) * mm});
            skLineSegment(sketch, "E950", {"start": v(-26.78, -7.29) * mm, "end": v(-26.72, -7) * mm});
            skLineSegment(sketch, "E951", {"start": v(-26.72, -7) * mm, "end": v(-26.64, -6.72) * mm});
            skLineSegment(sketch, "E952", {"start": v(-26.64, -6.72) * mm, "end": v(-26.56, -6.45) * mm});
            skLineSegment(sketch, "E953", {"start": v(-26.56, -6.45) * mm, "end": v(-26.46, -6.19) * mm});
            skLineSegment(sketch, "E954", {"start": v(-26.46, -6.19) * mm, "end": v(-26.35, -5.94) * mm});
            skLineSegment(sketch, "E955", {"start": v(-26.35, -5.94) * mm, "end": v(-26.22, -5.7) * mm});
            skLineSegment(sketch, "E956", {"start": v(-26.22, -5.7) * mm, "end": v(-26.08, -5.48) * mm});
            skLineSegment(sketch, "E957", {"start": v(-26.08, -5.48) * mm, "end": v(-25.91, -5.29) * mm});
            skLineSegment(sketch, "E958", {"start": v(-25.91, -5.29) * mm, "end": v(-25.74, -5.1) * mm});
            skLineSegment(sketch, "E959", {"start": v(-25.74, -5.1) * mm, "end": v(-25.66, -5) * mm});
            skLineSegment(sketch, "E960", {"start": v(-25.66, -5) * mm, "end": v(-25.6, -4.88) * mm});
            skLineSegment(sketch, "E961", {"start": v(-25.6, -4.88) * mm, "end": v(-25.53, -4.77) * mm});
            skLineSegment(sketch, "E962", {"start": v(-25.53, -4.77) * mm, "end": v(-25.48, -4.63) * mm});
            skLineSegment(sketch, "E963", {"start": v(-25.48, -4.63) * mm, "end": v(-25.46, -4.56) * mm});
            skLineSegment(sketch, "E964", {"start": v(-25.46, -4.56) * mm, "end": v(-25.44, -4.49) * mm});
            skLineSegment(sketch, "E965", {"start": v(-25.44, -4.49) * mm, "end": v(-25.43, -4.4) * mm});
            skLineSegment(sketch, "E966", {"start": v(-25.43, -4.4) * mm, "end": v(-25.44, -4.3) * mm});
            skLineSegment(sketch, "E967", {"start": v(-25.44, -4.3) * mm, "end": v(-25.54, -4.1) * mm});
            skLineSegment(sketch, "E968", {"start": v(-25.54, -4.1) * mm, "end": v(-26.12, -3.36) * mm});
            skLineSegment(sketch, "E969", {"start": v(-26.12, -3.36) * mm, "end": v(-26.64, -2.58) * mm});
            skLineSegment(sketch, "E970", {"start": v(-26.64, -2.58) * mm, "end": v(-26.8, -2.43) * mm});
            skLineSegment(sketch, "E971", {"start": v(-26.8, -2.43) * mm, "end": v(-26.9, -2.39) * mm});
            skLineSegment(sketch, "E972", {"start": v(-26.9, -2.39) * mm, "end": v(-26.98, -2.37) * mm});
            skLineSegment(sketch, "E973", {"start": v(-26.98, -2.37) * mm, "end": v(-27.06, -2.36) * mm});
            skLineSegment(sketch, "E974", {"start": v(-27.06, -2.36) * mm, "end": v(-27.13, -2.35) * mm});
            skLineSegment(sketch, "E975", {"start": v(-27.13, -2.35) * mm, "end": v(-27.27, -2.36) * mm});
            skLineSegment(sketch, "E976", {"start": v(-27.27, -2.36) * mm, "end": v(-27.4, -2.39) * mm});
            skLineSegment(sketch, "E977", {"start": v(-27.4, -2.39) * mm, "end": v(-27.53, -2.42) * mm});
            skLineSegment(sketch, "E978", {"start": v(-27.53, -2.42) * mm, "end": v(-27.66, -2.46) * mm});
            skLineSegment(sketch, "E979", {"start": v(-27.66, -2.46) * mm, "end": v(-27.89, -2.57) * mm});
            skLineSegment(sketch, "E980", {"start": v(-27.89, -2.57) * mm, "end": v(-28.13, -2.67) * mm});
            skLineSegment(sketch, "E981", {"start": v(-28.13, -2.67) * mm, "end": v(-28.38, -2.73) * mm});
            skLineSegment(sketch, "E982", {"start": v(-28.38, -2.73) * mm, "end": v(-28.64, -2.78) * mm});
            skLineSegment(sketch, "E983", {"start": v(-28.64, -2.78) * mm, "end": v(-28.91, -2.8) * mm});
            skLineSegment(sketch, "E984", {"start": v(-28.91, -2.8) * mm, "end": v(-29.2, -2.82) * mm});
            skLineSegment(sketch, "E985", {"start": v(-29.2, -2.82) * mm, "end": v(-29.48, -2.82) * mm});
            skLineSegment(sketch, "E986", {"start": v(-29.48, -2.82) * mm, "end": v(-29.77, -2.8) * mm});
            skLineSegment(sketch, "E987", {"start": v(-29.77, -2.8) * mm, "end": v(-30.06, -2.78) * mm});
            skLineSegment(sketch, "E988", {"start": v(-30.06, -2.78) * mm, "end": v(-30.36, -2.74) * mm});
            skLineSegment(sketch, "E989", {"start": v(-30.36, -2.74) * mm, "end": v(-30.66, -2.69) * mm});
            skLineSegment(sketch, "E990", {"start": v(-30.66, -2.69) * mm, "end": v(-30.89, -2.64) * mm});
            skLineSegment(sketch, "E991", {"start": v(-30.89, -2.64) * mm, "end": v(-31.61, -0.4) * mm});
            skLineSegment(sketch, "E992", {"start": v(-31.61, -0.4) * mm, "end": v(-31.45, -0.23) * mm});
            skLineSegment(sketch, "E993", {"start": v(-31.45, -0.23) * mm, "end": v(-31.24, -0.01) * mm});
            skLineSegment(sketch, "E994", {"start": v(-31.24, -0.01) * mm, "end": v(-31.02, 0.2) * mm});
            skLineSegment(sketch, "E995", {"start": v(-31.02, 0.2) * mm, "end": v(-30.8, 0.39) * mm});
            skLineSegment(sketch, "E996", {"start": v(-30.8, 0.39) * mm, "end": v(-30.58, 0.57) * mm});
            skLineSegment(sketch, "E997", {"start": v(-30.58, 0.57) * mm, "end": v(-30.35, 0.74) * mm});
            skLineSegment(sketch, "E998", {"start": v(-30.35, 0.74) * mm, "end": v(-30.11, 0.89) * mm});
            skLineSegment(sketch, "E999", {"start": v(-30.11, 0.89) * mm, "end": v(-29.88, 1.03) * mm});
            skLineSegment(sketch, "E1000", {"start": v(-29.88, 1.03) * mm, "end": v(-29.64, 1.14) * mm});
            skLineSegment(sketch, "E1001", {"start": v(-29.64, 1.14) * mm, "end": v(-29.4, 1.24) * mm});
            skLineSegment(sketch, "E1002", {"start": v(-29.4, 1.24) * mm, "end": v(-29.14, 1.3) * mm});
            skLineSegment(sketch, "E1003", {"start": v(-29.14, 1.3) * mm, "end": v(-28.9, 1.35) * mm});
            skLineSegment(sketch, "E1004", {"start": v(-28.9, 1.35) * mm, "end": v(-28.77, 1.39) * mm});
            skLineSegment(sketch, "E1005", {"start": v(-28.77, 1.39) * mm, "end": v(-28.65, 1.44) * mm});
            skLineSegment(sketch, "E1006", {"start": v(-28.65, 1.44) * mm, "end": v(-28.53, 1.5) * mm});
            skLineSegment(sketch, "E1007", {"start": v(-28.53, 1.5) * mm, "end": v(-28.4, 1.57) * mm});
            skLineSegment(sketch, "E1008", {"start": v(-28.4, 1.57) * mm, "end": v(-28.35, 1.62) * mm});
            skLineSegment(sketch, "E1009", {"start": v(-28.35, 1.62) * mm, "end": v(-28.3, 1.67) * mm});
            skLineSegment(sketch, "E1010", {"start": v(-28.3, 1.67) * mm, "end": v(-28.24, 1.74) * mm});
            skLineSegment(sketch, "E1011", {"start": v(-28.24, 1.74) * mm, "end": v(-28.18, 1.83) * mm});
            skLineSegment(sketch, "E1012", {"start": v(-28.18, 1.83) * mm, "end": v(-28.14, 2.04) * mm});
            skLineSegment(sketch, "E1013", {"start": v(-28.14, 2.04) * mm, "end": v(-28.18, 2.98) * mm});
            skLineSegment(sketch, "E1014", {"start": v(-28.18, 2.98) * mm, "end": v(-28.14, 3.92) * mm});
            skCircle(sketch, "E1015", {"center": v(-17.4, 2.98) * mm, "radius": 3.18 * mm});
            skCircle(sketch, "E1016", {"center": v(-50.41, 2.98) * mm, "radius": 7.07 * mm});
            skLineSegment(sketch, "E1017", {"start": v(-52.8, 21.33) * mm, "end": v(-52.76, 21.43) * mm});
            skLineSegment(sketch, "E1018", {"start": v(-32.06, 0.59) * mm, "end": v(-31.97, 0.63) * mm});
            skSolve(sketch);
        }
        {
            var Q0;
            {var subQ17=sQuery(id+"F0.wireOp",EDGE,"E485");Q0=makeQuery(id+"F0.imprint","IMPRINT",FACE,{"disambiguationData":[TD([[makeQuery(id+"F0.imprint","IMPRINT",EDGE,{"derivedFrom":subQ17}),-1.0]])]});}
            var Q1;
            Q1=makeQuery(id+"F0.imprint","IMPRINT",FACE,{"disambiguationData":[TD([[makeQuery(id+"F0.imprint","IMPRINT",EDGE,{"derivedFrom":sQuery(id+"F0.wireOp",EDGE,"E0")}),-1.0]])]});
            extrude(context, id + "F1", {"entities" : qUnion([Q0, Q1]), "depth" : 2.54 * mm, "offsetDistance" : 25.4 * mm});
        }
        {
            var Q0;
            Q0=makeQuery(id+"F1.opExtrude","CAP_FACE",FACE,{"disambiguationData":[OSD([sQuery(id+"F0.wireOp",EDGE,"E0"),sQuery(id+"F0.wireOp",EDGE,"E1"),sQuery(id+"F0.wireOp",EDGE,"E2"),sQuery(id+"F0.wireOp",EDGE,"E3"),sQuery(id+"F0.wireOp",EDGE,"E4"),sQuery(id+"F0.wireOp",EDGE,"E5"),sQuery(id+"F0.wireOp",EDGE,"E6"),sQuery(id+"F0.wireOp",EDGE,"E7"),sQuery(id+"F0.wireOp",EDGE,"E8"),sQuery(id+"F0.wireOp",EDGE,"E9"),sQuery(id+"F0.wireOp",EDGE,"E10"),sQuery(id+"F0.wireOp",EDGE,"E11"),sQuery(id+"F0.wireOp",EDGE,"E12"),sQuery(id+"F0.wireOp",EDGE,"E13"),sQuery(id+"F0.wireOp",EDGE,"E14"),sQuery(id+"F0.wireOp",EDGE,"E15"),sQuery(id+"F0.wireOp",EDGE,"E16"),sQuery(id+"F0.wireOp",EDGE,"E17"),sQuery(id+"F0.wireOp",EDGE,"E18"),sQuery(id+"F0.wireOp",EDGE,"E19"),sQuery(id+"F0.wireOp",EDGE,"E20"),sQuery(id+"F0.wireOp",EDGE,"E21"),sQuery(id+"F0.wireOp",EDGE,"E22"),sQuery(id+"F0.wireOp",EDGE,"E23"),sQuery(id+"F0.wireOp",EDGE,"E24"),sQuery(id+"F0.wireOp",EDGE,"E25"),sQuery(id+"F0.wireOp",EDGE,"E26"),sQuery(id+"F0.wireOp",EDGE,"E350"),sQuery(id+"F0.wireOp",EDGE,"E351"),sQuery(id+"F0.wireOp",EDGE,"E352"),sQuery(id+"F0.wireOp",EDGE,"E353"),sQuery(id+"F0.wireOp",EDGE,"E354"),sQuery(id+"F0.wireOp",EDGE,"E355"),sQuery(id+"F0.wireOp",EDGE,"E356"),sQuery(id+"F0.wireOp",EDGE,"E357"),sQuery(id+"F0.wireOp",EDGE,"E358"),sQuery(id+"F0.wireOp",EDGE,"E359"),sQuery(id+"F0.wireOp",EDGE,"E360"),sQuery(id+"F0.wireOp",EDGE,"E361"),sQuery(id+"F0.wireOp",EDGE,"E362"),sQuery(id+"F0.wireOp",EDGE,"E363"),sQuery(id+"F0.wireOp",EDGE,"E364"),sQuery(id+"F0.wireOp",EDGE,"E365"),sQuery(id+"F0.wireOp",EDGE,"E366"),sQuery(id+"F0.wireOp",EDGE,"E367"),sQuery(id+"F0.wireOp",EDGE,"E368"),sQuery(id+"F0.wireOp",EDGE,"E369"),sQuery(id+"F0.wireOp",EDGE,"E370"),sQuery(id+"F0.wireOp",EDGE,"E371"),sQuery(id+"F0.wireOp",EDGE,"E372"),sQuery(id+"F0.wireOp",EDGE,"E373"),sQuery(id+"F0.wireOp",EDGE,"E374"),sQuery(id+"F0.wireOp",EDGE,"E375"),sQuery(id+"F0.wireOp",EDGE,"E376"),sQuery(id+"F0.wireOp",EDGE,"E377"),sQuery(id+"F0.wireOp",EDGE,"E378"),sQuery(id+"F0.wireOp",EDGE,"E379"),sQuery(id+"F0.wireOp",EDGE,"E380"),sQuery(id+"F0.wireOp",EDGE,"E381"),sQuery(id+"F0.wireOp",EDGE,"E382"),sQuery(id+"F0.wireOp",EDGE,"E383"),sQuery(id+"F0.wireOp",EDGE,"E384"),sQuery(id+"F0.wireOp",EDGE,"E385"),sQuery(id+"F0.wireOp",EDGE,"E386"),sQuery(id+"F0.wireOp",EDGE,"E387"),sQuery(id+"F0.wireOp",EDGE,"E388"),sQuery(id+"F0.wireOp",EDGE,"E389"),sQuery(id+"F0.wireOp",EDGE,"E390"),sQuery(id+"F0.wireOp",EDGE,"E391"),sQuery(id+"F0.wireOp",EDGE,"E392"),sQuery(id+"F0.wireOp",EDGE,"E393"),sQuery(id+"F0.wireOp",EDGE,"E394"),sQuery(id+"F0.wireOp",EDGE,"E395"),sQuery(id+"F0.wireOp",EDGE,"E396"),sQuery(id+"F0.wireOp",EDGE,"E397"),sQuery(id+"F0.wireOp",EDGE,"E398"),sQuery(id+"F0.wireOp",EDGE,"E399"),sQuery(id+"F0.wireOp",EDGE,"E400"),sQuery(id+"F0.wireOp",EDGE,"E401"),sQuery(id+"F0.wireOp",EDGE,"E402"),sQuery(id+"F0.wireOp",EDGE,"E403"),sQuery(id+"F0.wireOp",EDGE,"E404"),sQuery(id+"F0.wireOp",EDGE,"E405"),sQuery(id+"F0.wireOp",EDGE,"E406"),sQuery(id+"F0.wireOp",EDGE,"E407"),sQuery(id+"F0.wireOp",EDGE,"E408"),sQuery(id+"F0.wireOp",EDGE,"E409"),sQuery(id+"F0.wireOp",EDGE,"E410"),sQuery(id+"F0.wireOp",EDGE,"E411"),sQuery(id+"F0.wireOp",EDGE,"E412"),sQuery(id+"F0.wireOp",EDGE,"E413"),sQuery(id+"F0.wireOp",EDGE,"E414"),sQuery(id+"F0.wireOp",EDGE,"E415"),sQuery(id+"F0.wireOp",EDGE,"E416"),sQuery(id+"F0.wireOp",EDGE,"E417"),sQuery(id+"F0.wireOp",EDGE,"E418"),sQuery(id+"F0.wireOp",EDGE,"E419"),sQuery(id+"F0.wireOp",EDGE,"E420"),sQuery(id+"F0.wireOp",EDGE,"E421"),sQuery(id+"F0.wireOp",EDGE,"E422"),sQuery(id+"F0.wireOp",EDGE,"E423"),sQuery(id+"F0.wireOp",EDGE,"E424"),sQuery(id+"F0.wireOp",EDGE,"E425"),sQuery(id+"F0.wireOp",EDGE,"E426"),sQuery(id+"F0.wireOp",EDGE,"E427"),sQuery(id+"F0.wireOp",EDGE,"E428"),sQuery(id+"F0.wireOp",EDGE,"E429"),sQuery(id+"F0.wireOp",EDGE,"E430"),sQuery(id+"F0.wireOp",EDGE,"E431"),sQuery(id+"F0.wireOp",EDGE,"E432"),sQuery(id+"F0.wireOp",EDGE,"E433"),sQuery(id+"F0.wireOp",EDGE,"E434"),sQuery(id+"F0.wireOp",EDGE,"E435"),sQuery(id+"F0.wireOp",EDGE,"E436"),sQuery(id+"F0.wireOp",EDGE,"E437"),sQuery(id+"F0.wireOp",EDGE,"E438"),sQuery(id+"F0.wireOp",EDGE,"E439"),sQuery(id+"F0.wireOp",EDGE,"E440"),sQuery(id+"F0.wireOp",EDGE,"E441"),sQuery(id+"F0.wireOp",EDGE,"E442"),sQuery(id+"F0.wireOp",EDGE,"E443"),sQuery(id+"F0.wireOp",EDGE,"E444"),sQuery(id+"F0.wireOp",EDGE,"E445"),sQuery(id+"F0.wireOp",EDGE,"E446"),sQuery(id+"F0.wireOp",EDGE,"E447"),sQuery(id+"F0.wireOp",EDGE,"E448"),sQuery(id+"F0.wireOp",EDGE,"E449"),sQuery(id+"F0.wireOp",EDGE,"E450"),sQuery(id+"F0.wireOp",EDGE,"E451"),sQuery(id+"F0.wireOp",EDGE,"E452"),sQuery(id+"F0.wireOp",EDGE,"E453"),sQuery(id+"F0.wireOp",EDGE,"E454"),sQuery(id+"F0.wireOp",EDGE,"E455"),sQuery(id+"F0.wireOp",EDGE,"E456"),sQuery(id+"F0.wireOp",EDGE,"E457"),sQuery(id+"F0.wireOp",EDGE,"E458"),sQuery(id+"F0.wireOp",EDGE,"E459"),sQuery(id+"F0.wireOp",EDGE,"E460"),sQuery(id+"F0.wireOp",EDGE,"E461"),sQuery(id+"F0.wireOp",EDGE,"E462"),sQuery(id+"F0.wireOp",EDGE,"E463"),sQuery(id+"F0.wireOp",EDGE,"E464"),sQuery(id+"F0.wireOp",EDGE,"E465"),sQuery(id+"F0.wireOp",EDGE,"E466"),sQuery(id+"F0.wireOp",EDGE,"E467"),sQuery(id+"F0.wireOp",EDGE,"E468"),sQuery(id+"F0.wireOp",EDGE,"E469"),sQuery(id+"F0.wireOp",EDGE,"E470"),sQuery(id+"F0.wireOp",EDGE,"E471"),sQuery(id+"F0.wireOp",EDGE,"E472"),sQuery(id+"F0.wireOp",EDGE,"E473"),sQuery(id+"F0.wireOp",EDGE,"E474"),sQuery(id+"F0.wireOp",EDGE,"E475"),sQuery(id+"F0.wireOp",EDGE,"E476"),sQuery(id+"F0.wireOp",EDGE,"E477"),sQuery(id+"F0.wireOp",EDGE,"E478"),sQuery(id+"F0.wireOp",EDGE,"E479"),sQuery(id+"F0.wireOp",EDGE,"E480"),sQuery(id+"F0.wireOp",EDGE,"E481"),sQuery(id+"F0.wireOp",EDGE,"E482"),sQuery(id+"F0.wireOp",EDGE,"E483"),sQuery(id+"F0.wireOp",EDGE,"E484"),sQuery(id+"F0.wireOp",EDGE,"E485"),sQuery(id+"F0.wireOp",EDGE,"E486"),sQuery(id+"F0.wireOp",EDGE,"E487"),sQuery(id+"F0.wireOp",EDGE,"E488"),sQuery(id+"F0.wireOp",EDGE,"E489"),sQuery(id+"F0.wireOp",EDGE,"E510"),sQuery(id+"F0.wireOp",EDGE,"E511"),sQuery(id+"F0.wireOp",EDGE,"E512"),sQuery(id+"F0.wireOp",EDGE,"E513"),sQuery(id+"F0.wireOp",EDGE,"E535"),sQuery(id+"F0.wireOp",EDGE,"E536"),sQuery(id+"F0.wireOp",EDGE,"E537"),sQuery(id+"F0.wireOp",EDGE,"E558"),sQuery(id+"F0.wireOp",EDGE,"E559"),sQuery(id+"F0.wireOp",EDGE,"E560"),sQuery(id+"F0.wireOp",EDGE,"E561"),sQuery(id+"F0.wireOp",EDGE,"E562"),sQuery(id+"F0.wireOp",EDGE,"E564"),sQuery(id+"F0.wireOp",EDGE,"E566"),sQuery(id+"F0.wireOp",EDGE,"E1011"),sQuery(id+"F0.wireOp",EDGE,"E1016"),sQuery(id+"F0.wireOp",EDGE,"E1017"),sQuery(id+"F0.wireOp",EDGE,"E1018")])],"isStart":false});
            var sketch = newSketch(context, id + "F2", { "sketchPlane" : qUnion([Q0])});
            skCircle(sketch, "E1019", {"center": v(-50.41, 2.98) * mm, "radius": 1.27 * mm});
            skSolve(sketch);
        }
        {
            var Q0;
            Q0=makeQuery(id+"F2.imprint","IMPRINT",FACE,{"disambiguationData":[TD([[makeQuery(id+"F2.imprint","IMPRINT",EDGE,{"derivedFrom":makeQuery(id+"F1.opExtrude","CAP_EDGE",EDGE,{"disambiguationData":[OSD([sQuery(id+"F0.wireOp",EDGE,"E0")])],"isStart":false})}),-1.0]])]});
            var Q1;
            Q1=makeQuery(id+"F2.imprint","IMPRINT",FACE,{"disambiguationData":[TD([[makeQuery(id+"F2.imprint","IMPRINT",EDGE,{"derivedFrom":sQuery(id+"F2.wireOp",EDGE,"E1019")}),-1.0]])]});
            extrude(context, id + "F3", {"entities" : qUnion([Q0, Q1]), "operationType" : NewBodyOperationType.ADD, "depth" : 1.27 * mm, "offsetDistance" : 25.4 * mm});
        }
        {
            var Q0;
            {var subQ12=sQuery(id+"F0.wireOp",EDGE,"E565");Q0=makeQuery(id+"F0.imprint","IMPRINT",FACE,{"disambiguationData":[TD([[makeQuery(id+"F0.imprint","IMPRINT",EDGE,{"derivedFrom":subQ12}),-1.0]])]});}
            extrude(context, id + "F4", {"entities" : qUnion([Q0]), "depth" : 3.8 * mm, "offsetDistance" : 25.4 * mm});
        }
        {
            var Q0;
            Q0=qCreatedBy(makeId("Right.planeOp"),FACE);
            var sketch = newSketch(context, id + "F5", { "sketchPlane" : qUnion([Q0])});
            skCircle(sketch, "E1020", {"center": v(0, 0) * mm, "radius": 3 * mm});
            skLineSegment(sketch, "E1021", {"start": v(0, 18.24) * mm, "end": v(0, -18.78) * mm});
            skSolve(sketch);
        }
        {
            var Q0;
            {var subQ0=sQuery(id+"F5.wireOp",EDGE,"E1021");var subQ1=sQuery(id+"F5.wireOp",EDGE,"E1020");var subQ2=makeQuery(id+"F5.imprint","INTERSECT",VERTEX,{"disambiguationData":[OD(0.0)],"derivedFrom":[subQ1,subQ0]});Q0=makeQuery(id+"F5.imprint","IMPRINT",FACE,{"disambiguationData":[TD([[makeQuery(id+"F5.imprint","IMPRINT",EDGE,{"disambiguationData":[TD([[subQ2,-1.0]])],"derivedFrom":subQ1}),1.0]])]});}
            extrude(context, id + "F6", {"entities" : qUnion([Q0]), "depth" : 7.62 * mm, "offsetDistance" : 25.4 * mm});
        }
        {
            var Q0;
            Q0=makeQuery(id+"F6.opExtrude","CAP_FACE",FACE,{"disambiguationData":[OSD([sQuery(id+"F5.wireOp",EDGE,"E1020"),sQuery(id+"F5.wireOp",EDGE,"E1021")])],"isStart":false});
            var sketch = newSketch(context, id + "F7", { "sketchPlane" : qUnion([Q0])});
            skArc(sketch, "E1022.0", {"start": v(0, -3) * mm, "mid": v(3, 0) * mm, "end": v(0, 3) * mm});
            skLineSegment(sketch, "E1022.1", {"start": v(0, 4) * mm, "end": v(0, -4) * mm});
            skCircle(sketch, "E1023", {"center": v(0, 0) * mm, "radius": 4 * mm});
            skSolve(sketch);
        }
        {
            var Q0;
            {var subQ0=sQuery(id+"F7.wireOp",EDGE,"E1022.0");Q0=makeQuery(id+"F7.imprint","IMPRINT",FACE,{"disambiguationData":[TD([[makeQuery(id+"F7.imprint","IMPRINT",EDGE,{"derivedFrom":subQ0}),-1.0]])]});}
            var Q1;
            {var subQ0=sQuery(id+"F7.wireOp",EDGE,"E1022.0");Q1=makeQuery(id+"F7.imprint","IMPRINT",FACE,{"disambiguationData":[TD([[makeQuery(id+"F7.imprint","IMPRINT",EDGE,{"derivedFrom":subQ0}),1.0]])]});}
            extrude(context, id + "F8", {"entities" : qUnion([Q0, Q1]), "operationType" : NewBodyOperationType.ADD, "depth" : 10.16 * mm, "offsetDistance" : 25.4 * mm});
        }
        {
            var Q0;
            Q0=makeQuery(id+"F8.opExtrude","CAP_FACE",FACE,{"disambiguationData":[OSD([sQuery(id+"F7.wireOp",EDGE,"E1022.1"),sQuery(id+"F7.wireOp",EDGE,"E1023")])],"isStart":false});
            var sketch = newSketch(context, id + "F9", { "sketchPlane" : qUnion([Q0])});
            skLineSegment(sketch, "E1024.bottom", {"start": v(1.02, 4) * mm, "end": v(-1.02, 4) * mm});
            skLineSegment(sketch, "E1024.top", {"start": v(1.02, -4) * mm, "end": v(-1.02, -4) * mm});
            skLineSegment(sketch, "E1024.left", {"start": v(1.02, 4) * mm, "end": v(1.02, -4) * mm});
            skLineSegment(sketch, "E1024.right", {"start": v(-1.02, 4) * mm, "end": v(-1.02, -4) * mm});
            skPoint(sketch, "E1024.middle", {"position": v(0, 0) * mm});
            skSolve(sketch);
        }
        {
            var Q0;
            {var subQ4=makeQuery(id+"F8.opExtrude","CAP_EDGE",EDGE,{"disambiguationData":[OSD([sQuery(id+"F7.wireOp",EDGE,"E1022.1")])],"isStart":false});Q0=makeQuery(id+"F9.imprint","IMPRINT",FACE,{"disambiguationData":[TD([[makeQuery(id+"F9.imprint","IMPRINT",EDGE,{"derivedFrom":subQ4}),1.0]])]});}
            extrude(context, id + "F10", {"entities" : qUnion([Q0]), "operationType" : NewBodyOperationType.REMOVE, "oppositeDirection" : true, "depth" : 6.35 * mm, "offsetDistance" : 25.4 * mm});
        }
        {
            var Q0;
            Q0=makeQuery(id+"F10.boolean.opBoolean","COPY",FACE,{"derivedFrom":makeQuery(id+"F10.opExtrude","SWEPT_FACE",FACE,{"disambiguationData":[OSD([sQuery(id+"F9.wireOp",EDGE,"E1024.left")])]})});
            var sketch = newSketch(context, id + "F11", { "sketchPlane" : qUnion([Q0])});
            skLineSegment(sketch, "E1025.bottom", {"start": v(11.43, 3.87) * mm, "end": v(13.46, 3.87) * mm});
            skLineSegment(sketch, "E1025.top", {"start": v(11.43, -3.87) * mm, "end": v(13.46, -3.87) * mm});
            skLineSegment(sketch, "E1025.left", {"start": v(11.43, 3.87) * mm, "end": v(11.43, -3.87) * mm});
            skLineSegment(sketch, "E1025.right", {"start": v(13.46, 3.87) * mm, "end": v(13.46, -3.87) * mm});
            skLineSegment(sketch, "E1026", {"start": v(13.46, 0) * mm, "end": v(11.43, 0) * mm});
            skSolve(sketch);
        }
        {
            var Q0;
            Q0=makeQuery(id+"F8.boolean.opBoolean","MERGE",FACE,{"derivedFrom":[makeQuery(id+"F6.opExtrude","SWEPT_FACE",FACE,{"disambiguationData":[OSD([sQuery(id+"F5.wireOp",EDGE,"E1021")])]}),makeQuery(id+"F8.opExtrude","SWEPT_FACE",FACE,{"disambiguationData":[OSD([sQuery(id+"F7.wireOp",EDGE,"E1022.1")])]})]});
            var sketch = newSketch(context, id + "F12", { "sketchPlane" : qUnion([Q0])});
            skLineSegment(sketch, "E1027", {"start": v(0, 0) * mm, "end": v(11.43, 0) * mm, "construction": true});
            skSolve(sketch);
        }
        {
            var Q0;
            {var subQ0=sQuery(id+"F11.wireOp",EDGE,"E1025.bottom");Q0=makeQuery(id+"F11.imprint","IMPRINT",FACE,{"disambiguationData":[TD([[makeQuery(id+"F11.imprint","IMPRINT",EDGE,{"derivedFrom":subQ0}),-1.0]])]});}
            var Q1;
            Q1=sQuery(id+"F12.wireOp",EDGE,"E1027");
            revolve(context, id + "F13", {"operationType" : NewBodyOperationType.REMOVE, "surfaceOperationType" : NewSurfaceOperationType.NEW, "entities" : qUnion([Q0]), "axis" : qUnion([Q1]), "revolveType" : RevolveType.ONE_DIRECTION, "oppositeDirection" : true, "angle" : 60 * degree});
        }
        {
            var Q0;
            Q0=makeQuery(id+"F13.boolean.opBoolean","COPY",EDGE,{"derivedFrom":makeQuery(id+"F13.opRevolve","CAP_EDGE",EDGE,{"disambiguationData":[OSD([sQuery(id+"F11.wireOp",EDGE,"E1025.left")]),OD(1.0)],"isStart":false})});
            var Q1;
            Q1=makeQuery(id+"F13.boolean.opBoolean","COPY",EDGE,{"derivedFrom":makeQuery(id+"F13.opRevolve","CAP_EDGE",EDGE,{"disambiguationData":[OSD([sQuery(id+"F11.wireOp",EDGE,"E1025.right")]),OD(1.0)],"isStart":false})});
            var Q2;
            Q2=makeQuery(id+"F10.boolean.opBoolean","COPY",EDGE,{"derivedFrom":makeQuery(id+"F10.opExtrude","CAP_EDGE",EDGE,{"disambiguationData":[OSD([sQuery(id+"F9.wireOp",EDGE,"E1024.left")])],"isStart":false})});
            var Q3;
            Q3=makeQuery(id+"F10.boolean.opBoolean","COPY",EDGE,{"derivedFrom":makeQuery(id+"F10.opExtrude","CAP_EDGE",EDGE,{"disambiguationData":[OSD([sQuery(id+"F9.wireOp",EDGE,"E1024.left")])],"isStart":true})});
            fillet(context, id + "F14", {"entities" : qUnion([Q0, Q1, Q2, Q3]), "radius" : 1.02 * mm, "tangentPropagation" : true, "allowEdgeOverflow" : false});
        }
    });
